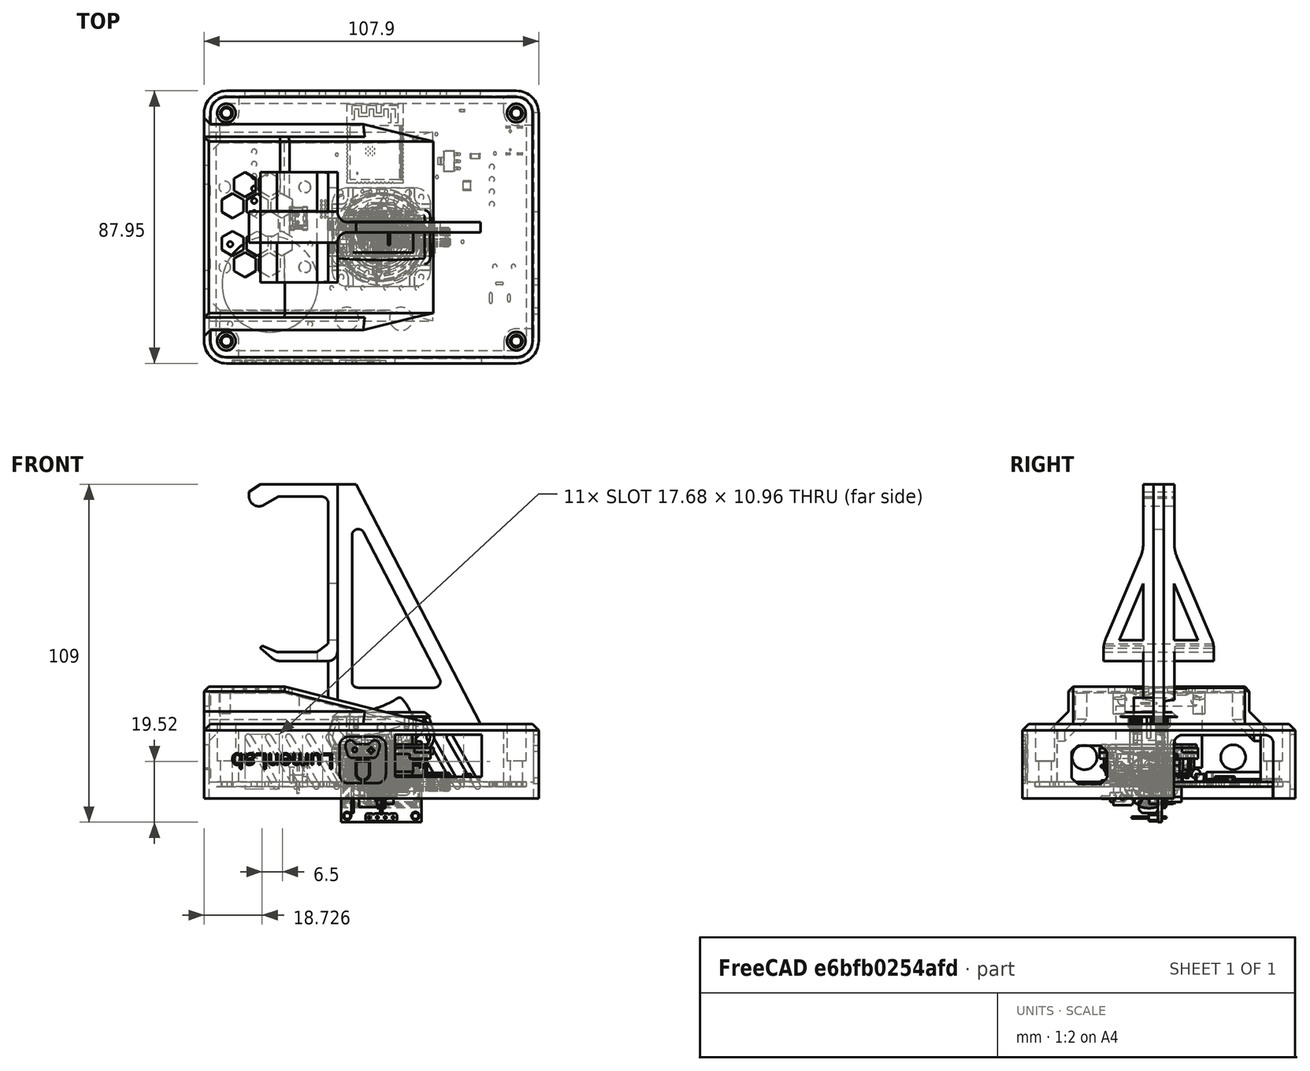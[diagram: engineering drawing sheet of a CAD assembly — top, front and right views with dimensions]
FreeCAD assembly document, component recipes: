
FREECAD ASSEMBLY — COMPONENT RECIPES ("lumenlab-enclosure-redesign")

This assembly document has 9 components, labeled P0..P8 below (a component is one placed body or linked part). 8 of them carry a construction recipe — the FreeCAD feature program that regenerates the part from scratch, quoted from this document or its linked companion documents; the rest are supplied as boundary geometry only. No exploded tour is included for this assembly.
COMPONENT P0 — geometry summary ("lumenlab-pcb001"; no construction recipe available for this part):
  bounding box: 99.9 x 79.9 x 1.6 mm
  tessellated surface: 20,328 triangles
  volume: 11234 mm^3 (88% of its bounding box)
  symmetry: mirror-symmetric across its z mid-plane
COMPONENT P1 — recipe-attached ("lid", modeled in this document).
Construction recipe (the document's own serialized feature program — sketch geometry with constraints, then the solid features built on it; lengths are millimeters unless a unit is written):

FEATURE [PartDesign::SubShapeBinder] Binder
  BindCopyOnChange = 0
  BindMode = 0
  ClaimChildren = false
  Context = -> Body [Binder.]
  Fuse = false
  MakeFace = true
  OffsetFill = false
  OffsetIntersection = false
  OffsetJoinType = 0
  OffsetOpenResult = false
  PartialLoad = false
  Refine = true
  Relative = true
  Support = -> [Board_aaa008]
  _Version = 2
FEATURE [Sketcher::SketchObject] Sketch
  ArcFitTolerance = 1e-06
  AttachmentOffset = pos=(0,0,3.75) rot=(0,0,1;0rad)
  AttachmentSupport = -> [Binder]
  ExternalGeometry = -> [Binder]
  ExternalTypes = [0]
  FullyConstrained = true
  MakeInternals = false
  MapMode = 5
  Placement = pos=(0,0,-5.3502) rot=(1,0,0;3.14159rad)
  _ExternalGeoVersion = 0
  sketch-geometry (10):
    g0: LineSegment StartX=-57.1492 StartY=33.5464 StartZ=0 EndX=-57.1492 EndY=-39.9989 EndZ=0
    g1: LineSegment StartX=-49.9485 StartY=-47.1996 StartZ=0 EndX=43.5501 EndY=-47.1996 EndZ=0
    g2: LineSegment StartX=50.7508 StartY=-39.9989 StartZ=0 EndX=50.7508 EndY=33.5464 EndZ=0
    g3: LineSegment StartX=43.5501 StartY=40.7472 StartZ=0 EndX=-49.9485 EndY=40.7472 EndZ=0
    g4: ArcOfCircle CenterX=-49.9485 CenterY=33.5464 CenterZ=0 NormalX=0 NormalY=0 NormalZ=1 AngleXU=0 Radius=7.20071 StartAngle=1.5708 EndAngle=3.14159
    g5: ArcOfCircle CenterX=-49.9485 CenterY=-39.9989 CenterZ=0 NormalX=0 NormalY=0 NormalZ=1 AngleXU=0 Radius=7.20071 StartAngle=3.14159 EndAngle=4.71239
    g6: ArcOfCircle CenterX=43.5501 CenterY=-39.9989 CenterZ=0 NormalX=0 NormalY=0 NormalZ=1 AngleXU=0 Radius=7.20071 StartAngle=4.71239 EndAngle=6.28319
    g7: ArcOfCircle CenterX=43.5501 CenterY=33.5464 CenterZ=0 NormalX=0 NormalY=0 NormalZ=1 AngleXU=0 Radius=7.20071 StartAngle=1e-16 EndAngle=1.5708
    g8: GeomPoint [constr] X=-57.1492 Y=40.7472 Z=0
    g9: GeomPoint [constr] X=50.7508 Y=-47.1996 Z=0
  constraints (23):
    c: Tangent(g0,g4) = -1.5708
    c: Tangent(g0,g5) = -1.5708
    c: Tangent(g1,g5) = -1.5708
    c: Tangent(g1,g6) = -1.5708
    c: Tangent(g2,g6) = -1.5708
    c: Tangent(g2,g7) = -1.5708
    c: Tangent(g3,g7) = -1.5708
    c: Tangent(g3,g4) = -1.5708
    c: Vertical(g0)
    c: Vertical(g2)
    c: Horizontal(g1)
    c: Horizontal(g3)
    c: Equal(g4,g5)
    c: Equal(g5,g6)
    c: Equal(g6,g7)
    c: PointOnObject(g8,g0)
    c: PointOnObject(g8,g3)
    c: PointOnObject(g9,g1)
    c: PointOnObject(g9,g2)
    c: DistanceX(g0,g-5) = 4  'enclosure-width'
    c: Coincident(g4,g-4)
    c: Distance(g-7,g2) = 4
    c: Distance(g-9,g1) = 4
FEATURE [PartDesign::Pad] Pad
  Direction = (0,0,-1)
  Length = 2
  Length2 = 10
  Profile = -> Sketch
  ReferenceAxis = -> Sketch [N_Axis]
  Refine = true
  SideType = 0
  Suppressed = false
  Type = 0
  Type2 = 0
FEATURE [Sketcher::SketchObject] Sketch001
  ArcFitTolerance = 1e-06
  AttachmentSupport = -> [Pad]
  ExternalGeometry = -> [Binder]
  ExternalTypes = [0]
  FullyConstrained = true
  MakeInternals = false
  MapMode = 5
  Placement = pos=(0,0,-5.3502) rot=(0,0,1;0rad)
  _ExternalGeoVersion = 0
  sketch-geometry (20):
    g0: LineSegment StartX=-55.15 StartY=39.9996 StartZ=0 EndX=-55.15 EndY=-33.5498 EndZ=0
    g1: LineSegment StartX=-49.95 StartY=-38.7498 StartZ=0 EndX=43.551 EndY=-38.7498 EndZ=0
    g2: LineSegment StartX=48.751 StartY=-33.5498 StartZ=0 EndX=48.751 EndY=39.9996 EndZ=0
    g3: LineSegment StartX=43.551 StartY=45.1996 StartZ=0 EndX=-49.95 EndY=45.1996 EndZ=0
    g4: ArcOfCircle CenterX=-49.95 CenterY=39.9996 CenterZ=0 NormalX=0 NormalY=0 NormalZ=1 AngleXU=0 Radius=5.19999 StartAngle=1.5708 EndAngle=3.14159
    g5: ArcOfCircle CenterX=-49.95 CenterY=-33.5498 CenterZ=0 NormalX=0 NormalY=0 NormalZ=1 AngleXU=0 Radius=5.19999 StartAngle=3.14159 EndAngle=4.71239
    g6: ArcOfCircle CenterX=43.551 CenterY=-33.5498 CenterZ=0 NormalX=0 NormalY=0 NormalZ=1 AngleXU=0 Radius=5.19999 StartAngle=4.71239 EndAngle=6.28319
    g7: ArcOfCircle CenterX=43.551 CenterY=39.9996 CenterZ=0 NormalX=0 NormalY=0 NormalZ=1 AngleXU=0 Radius=5.19999 StartAngle=5e-16 EndAngle=1.5708
    g8: GeomPoint [constr] X=-55.15 Y=45.1996 Z=0
    g9: GeomPoint [constr] X=48.751 Y=-38.7498 Z=0
    g10: LineSegment StartX=-53.35 StartY=39.9996 StartZ=0 EndX=-53.35 EndY=-33.5498 EndZ=0
    g11: LineSegment StartX=-49.95 StartY=-36.9498 StartZ=0 EndX=43.551 EndY=-36.9498 EndZ=0
    g12: LineSegment StartX=46.951 StartY=-33.5498 StartZ=0 EndX=46.951 EndY=39.9996 EndZ=0
    g13: LineSegment StartX=43.551 StartY=43.3996 StartZ=0 EndX=-49.95 EndY=43.3996 EndZ=0
    g14: ArcOfCircle CenterX=-49.95 CenterY=39.9996 CenterZ=0 NormalX=0 NormalY=0 NormalZ=1 AngleXU=0 Radius=3.39999 StartAngle=1.5708 EndAngle=3.14159
    g15: ArcOfCircle CenterX=-49.95 CenterY=-33.5498 CenterZ=0 NormalX=0 NormalY=0 NormalZ=1 AngleXU=0 Radius=3.39999 StartAngle=3.14159 EndAngle=4.71239
    g16: ArcOfCircle CenterX=43.551 CenterY=-33.5498 CenterZ=0 NormalX=0 NormalY=0 NormalZ=1 AngleXU=0 Radius=3.39999 StartAngle=4.71239 EndAngle=6.28319
    g17: ArcOfCircle CenterX=43.551 CenterY=39.9996 CenterZ=0 NormalX=0 NormalY=0 NormalZ=1 AngleXU=0 Radius=3.39999 StartAngle=0 EndAngle=1.5708
    g18: GeomPoint [constr] X=-53.35 Y=43.3996 Z=0
    g19: GeomPoint [constr] X=46.951 Y=-36.9498 Z=0
  constraints (46):
    c: Tangent(g0,g4) = -1.5708
    c: Tangent(g0,g5) = -1.5708
    c: Tangent(g1,g5) = -1.5708
    c: Tangent(g1,g6) = -1.5708
    c: Tangent(g2,g6) = -1.5708
    c: Tangent(g2,g7) = -1.5708
    c: Tangent(g3,g7) = -1.5708
    c: Tangent(g3,g4) = -1.5708
    c: Vertical(g0)
    c: Vertical(g2)
    c: Horizontal(g1)
    c: Horizontal(g3)
    c: Equal(g4,g5)
    c: Equal(g5,g6)
    c: Equal(g6,g7)
    c: PointOnObject(g8,g0)
    c: PointOnObject(g8,g3)
    c: PointOnObject(g9,g1)
    c: PointOnObject(g9,g2)
    c: DistanceX(g0,g-5) = 2
    c: Coincident(g4,g-4)
    c: DistanceX(g-7,g2) = 2
    c: DistanceY(g1,g-9) = 2
    c: Tangent(g10,g14) = -1.5708
    c: Tangent(g10,g15) = -1.5708
    c: Tangent(g11,g15) = -1.5708
    c: Tangent(g11,g16) = -1.5708
    c: Tangent(g12,g16) = -1.5708
    c: Tangent(g12,g17) = -1.5708
    c: Tangent(g13,g17) = -1.5708
    c: Tangent(g13,g14) = -1.5708
    c: Vertical(g10)
    c: Vertical(g12)
    c: Horizontal(g11)
    c: Horizontal(g13)
    c: Equal(g14,g15)
    c: Equal(g15,g16)
    c: Equal(g16,g17)
    c: PointOnObject(g18,g10)
    c: PointOnObject(g18,g13)
    c: PointOnObject(g19,g11)
    c: PointOnObject(g19,g12)
    c: DistanceX(g10,g-5) = 0.2
    c: DistanceX(g-7,g12) = 0.2
    c: DistanceY(g11,g-9) = 0.2
    c: Coincident(g14,g4)
FEATURE [PartDesign::Pad] Pad001
  BaseFeature = -> Pad
  Direction = (0,0,1)
  Length = 5
  Length2 = 10
  Profile = -> Sketch001
  ReferenceAxis = -> Sketch001 [N_Axis]
  Refine = true
  SideType = 0
  Suppressed = false
  Type = 0
  Type2 = 0
FEATURE [Sketcher::SketchObject] Sketch002
  ArcFitTolerance = 1e-06
  ExternalGeometry = -> [Binder,Pad001]
  ExternalTypes = [0]
  FullyConstrained = true
  MakeInternals = false
  MapMode = 5
  Placement = pos=(0,0,-2) rot=(1,0,0;3.14159rad)
  _ExternalGeoVersion = 0
  sketch-geometry (10):
    g0: LineSegment StartX=-53.1492 StartY=29.5498 StartZ=0 EndX=-53.35 EndY=29.5498 EndZ=0
    g1: LineSegment StartX=-45.95 StartY=36.7473 StartZ=0 EndX=-45.95 EndY=36.9498 EndZ=0
    g2: LineSegment StartX=-45.95 StartY=36.9498 StartZ=0 EndX=-49.95 EndY=36.9498 EndZ=0
    g3: LineSegment StartX=-53.35 StartY=29.5498 StartZ=0 EndX=-53.35 EndY=33.5498 EndZ=0
    g4: ArcOfCircle CenterX=-49.95 CenterY=33.5498 CenterZ=0 NormalX=0 NormalY=0 NormalZ=1 AngleXU=0 Radius=3.39999 StartAngle=1.5708 EndAngle=3.14159
    g5: LineSegment StartX=-53.1492 StartY=29.5498 StartZ=0 EndX=-48.6466 EndY=29.5498 EndZ=0
    g6: ArcOfCircle CenterX=-48.6466 CenterY=30.4451 CenterZ=0 NormalX=0 NormalY=0 NormalZ=1 AngleXU=0 Radius=0.895293 StartAngle=4.71239 EndAngle=5.38086
    g7: LineSegment StartX=-48.0918 StartY=29.7425 StartZ=0 EndX=-46.138 EndY=31.2855 EndZ=0
    g8: ArcOfCircle CenterX=-46.4444 CenterY=31.6735 CenterZ=0 NormalX=0 NormalY=0 NormalZ=1 AngleXU=0 Radius=0.494368 StartAngle=5.38086 EndAngle=6.28319
    g9: LineSegment StartX=-45.95 StartY=31.6735 StartZ=0 EndX=-45.95 EndY=36.7473 EndZ=0
  constraints (24):
    c: PointOnObject(g0,g-8)
    c: Horizontal(g0)
    c: PointOnObject(g1,g-7)
    c: Vertical(g1)
    c: Coincident(g2,g1)
    c: Coincident(g2,g-9)
    c: Coincident(g3,g0)
    c: Coincident(g3,g-9)
    c: Coincident(g4,g2)
    c: Coincident(g4,g3)
    c: PointOnObject(g0,g-10)
    c: PointOnObject(g1,g-11)
    c: DistanceY(g3,g3) = 4
    c: DistanceX(g2,g2) = 4
    c: Equal(g4,g-9)
    c: Coincident(g0,g5)
    c: Tangent(g5,g6) = -1.5708
    c: Tangent(g6,g7) = -1.5708
    c: Tangent(g7,g8) = -1.5708
    c: Tangent(g8,g9) = -1.5708
    c: Vertical(g9)
    c: Coincident(g9,g1)
    c: Horizontal(g5)
    c: Block(g7)
FEATURE [PartDesign::Pad] Pad002
  BaseFeature = -> Pad001
  Direction = (0,-1e-16,-1)
  Length = 10
  Length2 = 10
  Profile = -> Sketch002
  ReferenceAxis = -> Sketch002 [N_Axis]
  Refine = true
  SideType = 0
  Suppressed = false
  Type = 2
  Type2 = 0
FEATURE [PartDesign::Plane] DatumPlane
  AttachmentOffset = pos=(0,0,0) rot=(1,0,0;1.5708rad)
  AttachmentSupport = -> [Pad002]
  Length = 122.59
  MapMode = 45
  Placement = pos=(-3.1995,3.22491,-2.8502) rot=(1,0,0;1.5708rad)
  ResizeMode = 0
  Width = 64.6901
  expr: .AttachmentOffset.Rotation.Pitch = 0
FEATURE [PartDesign::Plane] DatumPlane001
  AttachmentOffset = pos=(0,0,0) rot=(1,0,0;1.5708rad)
  AttachmentSupport = -> [Pad002]
  Length = 101.209
  MapMode = 45
  Placement = pos=(-3.1995,3.22491,-2.8502) rot=(0.57735,0.57735,0.57735;2.0944rad)
  ResizeMode = 0
  Width = 63.2625
FEATURE [PartDesign::Line] DatumLine
  AttacherType = Attacher::AttachEngineLine
  AttachmentSupport = -> [DatumPlane001,DatumPlane]
  Length = 20
  MapMode = 30
  Placement = pos=(-3.1995,3.22491,-2.8502) rot=(0,1,0;3.14159rad)
  ResizeMode = 0
FEATURE [PartDesign::Mirrored] Mirrored
  BaseFeature = -> Pad002
  MirrorPlane = -> DatumPlane
  Originals = -> [Pad002]
  Refine = true
  Suppressed = false
  TransformMode = 0
FEATURE [PartDesign::Mirrored] Mirrored001
  BaseFeature = -> Mirrored
  MirrorPlane = -> DatumPlane001
  Originals = -> [Pad002]
  Refine = true
  Suppressed = false
  TransformMode = 0
FEATURE [PartDesign::PolarPattern] PolarPattern
  Angle = 360
  Axis = -> DatumLine
  BaseFeature = -> Mirrored001
  Mode = 0
  Occurrences = 2
  Offset = 120
  Originals = -> [Pad002]
  Refine = true
  Reversed = true
  SpacingPattern = [0]
  Spacings = [-1]
  Suppressed = false
  TransformMode = 0
FEATURE [Sketcher::SketchObject] Sketch003
  ArcFitTolerance = 1e-06
  AttachmentSupport = -> [PolarPattern]
  ExternalTypes = [0]
  FullyConstrained = true
  MakeInternals = false
  MapMode = 5
  Placement = pos=(0,0,-2) rot=(0,0,1;0rad)
  _ExternalGeoVersion = 0
  sketch-geometry (1):
    g0: Circle CenterX=-49.95 CenterY=-33.5498 CenterZ=0 NormalX=0 NormalY=0 NormalZ=1 AngleXU=0 Radius=2.425
  constraints (2):
    c: Coincident(g0,g-3)
    c: Diameter(g0) = 4.85
FEATURE [PartDesign::Pocket] Pocket
  BaseFeature = -> PolarPattern
  Direction = (0,0,-1)
  Length = 4.35
  Length2 = 5
  Profile = -> Sketch003
  ReferenceAxis = -> Sketch003 [N_Axis]
  Refine = true
  SideType = 0
  Suppressed = false
  Type = 0
  Type2 = 0
FEATURE [PartDesign::Mirrored] Mirrored002
  BaseFeature = -> Pocket
  MirrorPlane = -> DatumPlane
  Originals = -> [Pocket]
  Refine = true
  Suppressed = false
  TransformMode = 0
FEATURE [PartDesign::Mirrored] Mirrored003
  BaseFeature = -> Mirrored002
  MirrorPlane = -> DatumPlane001
  Originals = -> [Pocket]
  Refine = true
  Suppressed = false
  TransformMode = 0
FEATURE [PartDesign::PolarPattern] PolarPattern001
  Angle = 360
  Axis = -> DatumLine
  BaseFeature = -> Mirrored003
  Mode = 0
  Occurrences = 2
  Offset = 120
  Originals = -> [Pocket]
  Refine = true
  SpacingPattern = [0]
  Spacings = [-1]
  Suppressed = false
  TransformMode = 0
FEATURE [Sketcher::SketchObject] Sketch018
  ArcFitTolerance = 1e-06
  ExternalTypes = [0]
  FullyConstrained = true
  MakeInternals = false
  MapMode = 5
  Placement = pos=(48.751,0,0) rot=(0.57735,0.57735,0.57735;2.0944rad)
  _ExternalGeoVersion = 0
  sketch-geometry (4):
    g0: LineSegment StartX=8.59847 StartY=-0.350198 StartZ=0 EndX=8.59847 EndY=-5.3502 EndZ=0
    g1: LineSegment StartX=8.59847 StartY=-5.3502 StartZ=0 EndX=39.3209 EndY=-5.3502 EndZ=0
    g2: LineSegment StartX=39.3209 StartY=-0.350198 StartZ=0 EndX=8.59847 EndY=-0.350198 EndZ=0
    g3: LineSegment StartX=39.3209 StartY=-5.3502 StartZ=0 EndX=39.3209 EndY=-0.350198 EndZ=0
  constraints (12):
    c: Coincident(g0,g1)
    c: Coincident(g2,g0)
    c: Vertical(g0)
    c: Horizontal(g1)
    c: Horizontal(g2)
    c: PointOnObject(g0,g-5)
    c: Distance(g0,g-3) = 0.1
    c: DistanceY(g0,g0) = 5
    c: Vertical(g3)
    c: Distance(g3,g-7) = 3.65
    c: Coincident(g1,g3)
    c: Coincident(g3,g2)
FEATURE [PartDesign::Pad] Pad007
  BaseFeature = -> PolarPattern001
  Direction = (1,1e-16,-1e-16)
  Length = 2
  Length2 = 10
  Profile = -> Sketch018
  ReferenceAxis = -> Sketch018 [N_Axis]
  Refine = true
  SideType = 0
  Suppressed = false
  Type = 0
  Type2 = 0
FEATURE [Sketcher::SketchObject] Sketch019
  ArcFitTolerance = 1e-06
  AttachmentSupport = -> [Pad007]
  ExternalTypes = [0]
  FullyConstrained = true
  MakeInternals = false
  MapMode = 5
  Placement = pos=(48.751,0,0) rot=(0.57735,0.57735,0.57735;2.0944rad)
  _ExternalGeoVersion = 0
  sketch-geometry (10):
    g0: LineSegment StartX=22.9809 StartY=2.01 StartZ=0 EndX=22.9809 EndY=1.3 EndZ=0
    g1: LineSegment StartX=28.0309 StartY=-3.75 StartZ=0 EndX=34.3709 EndY=-3.75 EndZ=0
    g2: LineSegment StartX=39.4209 StartY=1.3 StartZ=0 EndX=39.4209 EndY=2.01 EndZ=0
    g3: LineSegment StartX=34.3709 StartY=7.06 StartZ=0 EndX=28.0309 EndY=7.06 EndZ=0
    g4: ArcOfCircle CenterX=28.0309 CenterY=2.01 CenterZ=0 NormalX=0 NormalY=0 NormalZ=1 AngleXU=0 Radius=5.05 StartAngle=1.5708 EndAngle=3.14159
    g5: ArcOfCircle CenterX=28.0309 CenterY=1.3 CenterZ=0 NormalX=0 NormalY=0 NormalZ=1 AngleXU=0 Radius=5.05 StartAngle=3.14159 EndAngle=4.71239
    g6: ArcOfCircle CenterX=34.3709 CenterY=1.3 CenterZ=0 NormalX=0 NormalY=0 NormalZ=1 AngleXU=0 Radius=5.05 StartAngle=4.71239 EndAngle=6.28319
    g7: ArcOfCircle CenterX=34.3709 CenterY=2.01 CenterZ=0 NormalX=0 NormalY=0 NormalZ=1 AngleXU=0 Radius=5.05 StartAngle=0 EndAngle=1.5708
    g8: GeomPoint [constr] X=22.9809 Y=7.06 Z=0
    g9: GeomPoint [constr] X=39.4209 Y=-3.75 Z=0
  constraints (21):
    c: Tangent(g0,g4) = -1.5708
    c: Tangent(g0,g5) = -1.5708
    c: Tangent(g1,g5) = -1.5708
    c: Tangent(g1,g6) = -1.5708
    c: Tangent(g2,g6) = -1.5708
    c: Tangent(g2,g7) = -1.5708
    c: Tangent(g3,g7) = -1.5708
    c: Tangent(g3,g4) = -1.5708
    c: Vertical(g0)
    c: Vertical(g2)
    c: Horizontal(g1)
    c: Horizontal(g3)
    c: Equal(g5,g6)
    c: PointOnObject(g8,g0)
    c: PointOnObject(g8,g3)
    c: PointOnObject(g9,g1)
    c: PointOnObject(g9,g2)
    c: Coincident(g4,g-4)
    c: Coincident(g5,g-10)
    c: Coincident(g7,g-6)
    c: DistanceX(g0,g-4) = 3.75
FEATURE [PartDesign::Pocket] Pocket011
  BaseFeature = -> Pad007
  Direction = (-1,0,0)
  Length = 4
  Length2 = 5
  Profile = -> Sketch019
  ReferenceAxis = -> Sketch019 [N_Axis]
  Refine = true
  SideType = 2
  Suppressed = false
  Type = 0
  Type2 = 0
FEATURE [PartDesign::Chamfer] Chamfer006
  Angle = 45
  Base = -> Pocket011 [Edge30,Edge29,Edge28,Edge31,Edge32,Edge10,Edge4,Edge7]
  BaseFeature = -> Pocket011
  ChamferType = 0
  FlipDirection = false
  Refine = true
  Size = 1
  Size2 = 1
  SupportTransform = false
  Suppressed = false
  UseAllEdges = false
FEATURE [PartDesign::Body] Body  label="lid"
  AllowCompound = false
  Group = -> [Binder,Sketch,Pad,Sketch001,Pad001,Sketch002,Pad002,DatumPlane,Mirrored,DatumPlane001,Mirrored001,DatumLine,PolarPattern,Sketch003,Pocket,Mirrored002,Mirrored003,PolarPattern001,Sketch018,Pad007,Sketch019,Pocket011,Chamfer006]
  Origin = -> Origin032
  Tip = -> Chamfer006
COMPONENT P2 — recipe-attached ("Body", modeled in this document).
Construction recipe (the document's own serialized feature program — sketch geometry with constraints, then the solid features built on it; lengths are millimeters unless a unit is written):

FEATURE [PartDesign::SubShapeBinder] Binder001
  BindCopyOnChange = 0
  BindMode = 0
  ClaimChildren = false
  Context = -> Body001 [Binder001.]
  Fuse = false
  MakeFace = true
  OffsetFill = false
  OffsetIntersection = false
  OffsetJoinType = 0
  OffsetOpenResult = false
  PartialLoad = false
  Refine = true
  Relative = true
  Support = -> [Board_aaa008]
  _Version = 2
FEATURE [Sketcher::SketchObject] Sketch010
  ArcFitTolerance = 1e-06
  AttachmentOffset = pos=(0,0,3.75) rot=(0,0,1;0rad)
  AttachmentSupport = -> [Binder001]
  ExternalGeometry = -> [Binder001]
  ExternalTypes = [0]
  FullyConstrained = true
  MakeInternals = false
  MapMode = 5
  Placement = pos=(0,0,-5.3502) rot=(1,0,0;3.14159rad)
  _ExternalGeoVersion = 0
  sketch-geometry (19):
    g0: LineSegment StartX=-57.1492 StartY=33.5464 StartZ=0 EndX=-57.1492 EndY=-39.9996 EndZ=0
    g1: LineSegment StartX=-49.9492 StartY=-47.1996 StartZ=0 EndX=43.5508 EndY=-47.1996 EndZ=0
    g2: LineSegment StartX=50.7508 StartY=-39.9996 StartZ=0 EndX=50.7508 EndY=33.5464 EndZ=0
    g3: LineSegment StartX=43.5508 StartY=40.7464 StartZ=0 EndX=-49.9492 EndY=40.7464 EndZ=0
    g4: ArcOfCircle CenterX=-49.9492 CenterY=33.5464 CenterZ=0 NormalX=0 NormalY=0 NormalZ=1 AngleXU=0 Radius=7.19996 StartAngle=1.5708 EndAngle=3.14159
    g5: ArcOfCircle CenterX=-49.9492 CenterY=-39.9996 CenterZ=0 NormalX=0 NormalY=0 NormalZ=1 AngleXU=0 Radius=7.19996 StartAngle=3.14159 EndAngle=4.71239
    g6: ArcOfCircle CenterX=43.5508 CenterY=-39.9996 CenterZ=0 NormalX=0 NormalY=0 NormalZ=1 AngleXU=0 Radius=7.19996 StartAngle=4.71239 EndAngle=6.28319
    g7: ArcOfCircle CenterX=43.5508 CenterY=33.5464 CenterZ=0 NormalX=0 NormalY=0 NormalZ=1 AngleXU=0 Radius=7.19996 StartAngle=0 EndAngle=1.5708
    g8: GeomPoint [constr] X=-57.1492 Y=40.7464 Z=0
    g9: GeomPoint [constr] X=50.7508 Y=-47.1996 Z=0
    g10: LineSegment StartX=-49.9492 StartY=-45.5996 StartZ=0 EndX=43.5508 EndY=-45.5996 EndZ=0
    g11: LineSegment StartX=49.1508 StartY=-39.9996 StartZ=0 EndX=49.1508 EndY=33.5464 EndZ=0
    g12: LineSegment StartX=43.5508 StartY=39.1464 StartZ=0 EndX=-49.9492 EndY=39.1464 EndZ=0
    g13: LineSegment StartX=-55.5492 StartY=33.5464 StartZ=0 EndX=-55.5492 EndY=-39.9996 EndZ=0
    g14: ArcOfCircle CenterX=-49.9492 CenterY=-39.9996 CenterZ=0 NormalX=0 NormalY=0 NormalZ=1 AngleXU=0 Radius=5.59996 StartAngle=3.14159 EndAngle=4.71239
    g15: ArcOfCircle CenterX=43.5508 CenterY=-39.9996 CenterZ=0 NormalX=0 NormalY=0 NormalZ=1 AngleXU=0 Radius=5.59996 StartAngle=4.71239 EndAngle=6.28319
    g16: ArcOfCircle CenterX=43.5508 CenterY=33.5464 CenterZ=0 NormalX=0 NormalY=0 NormalZ=1 AngleXU=0 Radius=5.59996 StartAngle=4e-16 EndAngle=1.5708
    g17: ArcOfCircle CenterX=-49.9492 CenterY=33.5464 CenterZ=0 NormalX=0 NormalY=0 NormalZ=1 AngleXU=0 Radius=5.59996 StartAngle=1.5708 EndAngle=3.14159
    g18: GeomPoint [constr] X=-55.5492 Y=-45.5996 Z=0
  constraints (43):
    c: Tangent(g0,g4) = -1.5708
    c: Tangent(g0,g5) = -1.5708
    c: Tangent(g1,g5) = -1.5708
    c: Tangent(g1,g6) = -1.5708
    c: Tangent(g2,g6) = -1.5708
    c: Tangent(g2,g7) = -1.5708
    c: Tangent(g3,g7) = -1.5708
    c: Tangent(g3,g4) = -1.5708
    c: Vertical(g0)
    c: Vertical(g2)
    c: Horizontal(g1)
    c: Horizontal(g3)
    c: Equal(g4,g5)
    c: Equal(g5,g6)
    c: Equal(g6,g7)
    c: PointOnObject(g8,g0)
    c: PointOnObject(g8,g3)
    c: PointOnObject(g9,g1)
    c: PointOnObject(g9,g2)
    c: Distance(g0,g-3) = 4
    c: Coincident(g-10,g4)
    c: Distance(g2,g-7) = 4
    c: Distance(g1,g-4) = 4
    c: Tangent(g10,g14) = -1.5708
    c: Tangent(g10,g15) = -1.5708
    c: Tangent(g11,g15) = -1.5708
    c: Tangent(g11,g16) = -1.5708
    c: Tangent(g12,g16) = -1.5708
    c: Tangent(g12,g17) = -1.5708
    c: Tangent(g13,g17) = -1.5708
    c: Tangent(g13,g14) = -1.5708
    c: Horizontal(g10)
    c: Horizontal(g12)
    c: Vertical(g11)
    c: Vertical(g13)
    c: Equal(g14,g15)
    c: Equal(g15,g16)
    c: Equal(g16,g17)
    c: PointOnObject(g18,g10)
    c: PointOnObject(g18,g13)
    c: Distance(g0,g13) = 1.6
    c: Coincident(g14,g5)
    c: Coincident(g16,g7)
FEATURE [PartDesign::Pad] Pad003
  Direction = (0,0,-1)
  Length = 22
  Length2 = 10
  Profile = -> Sketch010
  ReferenceAxis = -> Sketch010 [N_Axis]
  Refine = true
  Reversed = true
  SideType = 0
  Suppressed = false
  Type = 0
  Type2 = 0
FEATURE [Sketcher::SketchObject] Sketch011
  ArcFitTolerance = 1e-06
  AttachmentSupport = -> [Pad003]
  ExternalGeometry = -> [Pad003]
  ExternalTypes = [0]
  FullyConstrained = true
  MakeInternals = false
  MapMode = 5
  Placement = pos=(0,0,16.6498) rot=(0,0,1;0rad)
  _ExternalGeoVersion = 0
  sketch-geometry (10):
    g0: LineSegment StartX=-57.1492 StartY=39.9996 StartZ=0 EndX=-57.1492 EndY=-33.5464 EndZ=0
    g1: LineSegment StartX=-49.9492 StartY=-40.7464 StartZ=0 EndX=43.5508 EndY=-40.7464 EndZ=0
    g2: LineSegment StartX=50.7508 StartY=-33.5464 StartZ=0 EndX=50.7508 EndY=39.9996 EndZ=0
    g3: LineSegment StartX=43.5508 StartY=47.1996 StartZ=0 EndX=-49.9492 EndY=47.1996 EndZ=0
    g4: ArcOfCircle CenterX=-49.9492 CenterY=39.9996 CenterZ=0 NormalX=0 NormalY=0 NormalZ=1 AngleXU=0 Radius=7.19996 StartAngle=1.5708 EndAngle=3.14159
    g5: ArcOfCircle CenterX=-49.9492 CenterY=-33.5464 CenterZ=0 NormalX=0 NormalY=0 NormalZ=1 AngleXU=0 Radius=7.19996 StartAngle=3.14159 EndAngle=4.71239
    g6: ArcOfCircle CenterX=43.5508 CenterY=-33.5464 CenterZ=0 NormalX=0 NormalY=0 NormalZ=1 AngleXU=0 Radius=7.19996 StartAngle=4.71239 EndAngle=6.28319
    g7: ArcOfCircle CenterX=43.5508 CenterY=39.9996 CenterZ=0 NormalX=0 NormalY=0 NormalZ=1 AngleXU=0 Radius=7.19996 StartAngle=0 EndAngle=1.5708
    g8: GeomPoint [constr] X=-57.1492 Y=47.1996 Z=0
    g9: GeomPoint [constr] X=50.7508 Y=-40.7464 Z=0
  constraints (20):
    c: Tangent(g0,g4) = -1.5708
    c: Tangent(g0,g5) = -1.5708
    c: Tangent(g1,g5) = -1.5708
    c: Tangent(g1,g6) = -1.5708
    c: Tangent(g2,g6) = -1.5708
    c: Tangent(g2,g7) = -1.5708
    c: Tangent(g3,g7) = -1.5708
    c: Tangent(g3,g4) = -1.5708
    c: Vertical(g2)
    c: Horizontal(g1)
    c: Equal(g4,g5)
    c: Equal(g5,g6)
    c: PointOnObject(g8,g0)
    c: PointOnObject(g8,g3)
    c: PointOnObject(g9,g1)
    c: PointOnObject(g9,g2)
    c: Coincident(g-5,g0)
    c: Coincident(g3,g-4)
    c: Coincident(g3,g-6)
    c: Coincident(g1,g-9)
FEATURE [PartDesign::Pad] Pad004
  BaseFeature = -> Pad003
  Direction = (0,0,1)
  Length = 2
  Length2 = 10
  Profile = -> Sketch011
  ReferenceAxis = -> Sketch011 [N_Axis]
  Refine = true
  SideType = 0
  Suppressed = false
  Type = 0
  Type2 = 0
FEATURE [Sketcher::SketchObject] Sketch013
  ArcFitTolerance = 1e-06
  ExternalTypes = [0]
  FullyConstrained = false
  MakeInternals = false
  MapMode = 5
  Placement = pos=(50.7508,0,3.061e-13) rot=(0.57735,0.57735,0.57735;2.0944rad)
  _ExternalGeoVersion = 0
  sketch-geometry (6):
    g0: LineSegment StartX=8.16428 StartY=12.4216 StartZ=0 EndX=8.16428 EndY=-5.3502 EndZ=0
    g1: LineSegment StartX=40.1456 StartY=12.4216 StartZ=0 EndX=40.1456 EndY=-5.3502 EndZ=0
    g2: LineSegment StartX=40.1456 StartY=-5.3502 StartZ=0 EndX=8.16428 EndY=-5.3502 EndZ=0
    g3: LineSegment StartX=10.823 StartY=15.0803 StartZ=0 EndX=37.4869 EndY=15.0803 EndZ=0
    g4: ArcOfCircle CenterX=10.823 CenterY=12.4216 CenterZ=0 NormalX=0 NormalY=0 NormalZ=1 AngleXU=0 Radius=2.6587 StartAngle=1.5708 EndAngle=3.14159
    g5: ArcOfCircle CenterX=37.4869 CenterY=12.4216 CenterZ=0 NormalX=0 NormalY=0 NormalZ=1 AngleXU=0 Radius=2.6587 StartAngle=1e-16 EndAngle=1.5708
  constraints (16):
    c: Vertical(g1)
    c: Coincident(g1,g2)
    c: PointOnObject(g0,g-10)
    c: Horizontal(g2)
    c: Coincident(g2,g0)
    c: Horizontal(g3)
    c: Vertical(g0)
    c: Coincident(g4,g0)
    c: Coincident(g3,g4)
    c: Coincident(g5,g3)
    c: Vertical(g3,g4)
    c: Horizontal(g0,g4)
    c: Coincident(g1,g5)
    c: Equal(g4,g5)
    c: Vertical(g3,g5)
    c: Horizontal(g5,g1)
FEATURE [PartDesign::Pocket] Pocket008
  BaseFeature = -> Pad004
  Direction = (-1,-1e-16,-5.9e-15)
  Length = 5
  Length2 = 5
  Profile = -> Sketch013
  ReferenceAxis = -> Sketch013 [N_Axis]
  Refine = true
  SideType = 0
  Suppressed = false
  Type = 2
  Type2 = 0
FEATURE [Sketcher::SketchObject] Sketch014
  ArcFitTolerance = 1e-06
  ExternalTypes = [0]
  FullyConstrained = true
  MakeInternals = false
  MapMode = 5
  Placement = pos=(50.7508,0,2.944e-13) rot=(0.57735,0.57735,0.57735;2.0944rad)
  _ExternalGeoVersion = 0
  sketch-geometry (4):
    g0: LineSegment StartX=-24.8504 StartY=11.7 StartZ=0 EndX=-24.8504 EndY=-0.7 EndZ=0
    g1: LineSegment StartX=-24.8504 StartY=-0.7 StartZ=0 EndX=-13.4504 EndY=-0.7 EndZ=0
    g2: LineSegment StartX=-13.4504 StartY=-0.7 StartZ=0 EndX=-13.4504 EndY=11.7 EndZ=0
    g3: LineSegment StartX=-13.4504 StartY=11.7 StartZ=0 EndX=-24.8504 EndY=11.7 EndZ=0
  constraints (12):
    c: Coincident(g0,g1)
    c: Coincident(g1,g2)
    c: Coincident(g2,g3)
    c: Coincident(g3,g0)
    c: Vertical(g0)
    c: Vertical(g2)
    c: Horizontal(g1)
    c: Horizontal(g3)
    c: Distance(g-5,g0) = 1
    c: Distance(g-6,g2) = 2
    c: Distance(g3,g-5) = 1
    c: Distance(g-4,g1) = 1
FEATURE [PartDesign::Pocket] Pocket009
  BaseFeature = -> Pocket008
  Direction = (-1,0,-5.8e-15)
  Length = 5
  Length2 = 5
  Profile = -> Sketch014
  ReferenceAxis = -> Sketch014 [N_Axis]
  Refine = true
  SideType = 0
  Suppressed = false
  Type = 2
  Type2 = 0
FEATURE [PartDesign::Chamfer] Chamfer004
  Angle = 45
  Base = -> Pocket009 [Edge57,Edge60,Edge55,Edge58]
  BaseFeature = -> Pocket009
  ChamferType = 0
  FlipDirection = false
  Refine = true
  Size = 2
  Size2 = 1
  SupportTransform = false
  Suppressed = false
  UseAllEdges = false
FEATURE [Sketcher::SketchObject] Sketch015
  ArcFitTolerance = 1e-06
  ExternalGeometry = -> [Binder001,Chamfer004]
  ExternalTypes = [0]
  FullyConstrained = true
  MakeInternals = false
  MapMode = 5
  Placement = pos=(0,0,0) rot=(1,0,0;3.14159rad)
  _ExternalGeoVersion = 0
  sketch-geometry (30):
    g0: LineSegment StartX=-55.5492 StartY=29.5464 StartZ=0 EndX=-49.9492 EndY=29.5464 EndZ=0
    g1: ArcOfCircle CenterX=-49.9492 CenterY=33.5464 CenterZ=0 NormalX=0 NormalY=0 NormalZ=1 AngleXU=0 Radius=4 StartAngle=4.71239 EndAngle=6.28319
    g2: LineSegment StartX=-45.9492 StartY=33.5464 StartZ=0 EndX=-45.9492 EndY=39.1464 EndZ=0
    g3: LineSegment StartX=-45.9492 StartY=39.1464 StartZ=0 EndX=-49.9492 EndY=39.1464 EndZ=0
    g4: ArcOfCircle CenterX=-49.9492 CenterY=33.5464 CenterZ=0 NormalX=0 NormalY=0 NormalZ=1 AngleXU=0 Radius=5.59996 StartAngle=1.5708 EndAngle=3.14159
    g5: LineSegment StartX=-55.5492 StartY=33.5464 StartZ=0 EndX=-55.5492 EndY=29.5464 EndZ=0
    g6: Circle CenterX=-49.9492 CenterY=33.5464 CenterZ=0 NormalX=0 NormalY=0 NormalZ=1 AngleXU=0 Radius=2
    g7: Circle CenterX=-49.9492 CenterY=-39.9996 CenterZ=0 NormalX=0 NormalY=0 NormalZ=1 AngleXU=0 Radius=2
    g8: LineSegment StartX=-49.9492 StartY=-35.9996 StartZ=0 EndX=-55.5492 EndY=-35.9996 EndZ=0
    g9: LineSegment [constr] StartX=-55.5492 StartY=-39.9996 StartZ=0 EndX=-55.5492 EndY=-4.52586 EndZ=0
    g10: LineSegment StartX=-55.5492 StartY=-35.9996 StartZ=0 EndX=-55.5492 EndY=-39.9996 EndZ=0
    g11: ArcOfCircle CenterX=-49.9492 CenterY=-39.9996 CenterZ=0 NormalX=0 NormalY=0 NormalZ=1 AngleXU=0 Radius=5.59996 StartAngle=3.14159 EndAngle=4.71239
    g12: LineSegment StartX=-49.9492 StartY=-45.5996 StartZ=0 EndX=-45.9492 EndY=-45.5996 EndZ=0
    g13: LineSegment [constr] StartX=49.1508 StartY=-39.9996 StartZ=0 EndX=49.1508 EndY=-8.19439 EndZ=0
    g14: LineSegment StartX=43.5508 StartY=-45.5996 StartZ=0 EndX=39.5508 EndY=-45.5996 EndZ=0
    g15: LineSegment StartX=43.5508 StartY=-35.9996 StartZ=0 EndX=49.1508 EndY=-35.9996 EndZ=0
    g16: LineSegment StartX=49.1508 StartY=-35.9996 StartZ=0 EndX=49.1508 EndY=-39.9996 EndZ=0
    g17: ArcOfCircle CenterX=43.5508 CenterY=-39.9996 CenterZ=0 NormalX=0 NormalY=0 NormalZ=1 AngleXU=0 Radius=5.59996 StartAngle=4.71239 EndAngle=6.28319
    g18: Circle CenterX=43.551 CenterY=-39.9996 CenterZ=0 NormalX=0 NormalY=0 NormalZ=1 AngleXU=0 Radius=2
    g19: Circle CenterX=43.5508 CenterY=33.5498 CenterZ=0 NormalX=0 NormalY=0 NormalZ=1 AngleXU=0 Radius=2
    g20: LineSegment StartX=39.5508 StartY=39.1464 StartZ=0 EndX=39.5508 EndY=33.5498 EndZ=0
    g21: ArcOfCircle CenterX=43.5508 CenterY=33.5498 CenterZ=0 NormalX=0 NormalY=0 NormalZ=1 AngleXU=0 Radius=4 StartAngle=3.14158 EndAngle=4.7124
    g22: LineSegment StartX=43.5508 StartY=29.5498 StartZ=0 EndX=49.1508 EndY=29.5498 EndZ=0
    g23: LineSegment StartX=49.1508 StartY=29.5498 StartZ=0 EndX=49.1508 EndY=33.5464 EndZ=0
    g24: ArcOfCircle CenterX=43.5508 CenterY=33.5464 CenterZ=0 NormalX=0 NormalY=0 NormalZ=1 AngleXU=0 Radius=5.59996 StartAngle=0 EndAngle=1.5708
    g25: LineSegment StartX=39.5508 StartY=39.1464 StartZ=0 EndX=43.5508 EndY=39.1464 EndZ=0
    g26: ArcOfCircle CenterX=-49.9492 CenterY=-39.9996 CenterZ=0 NormalX=0 NormalY=0 NormalZ=1 AngleXU=0 Radius=4 StartAngle=-1.8e-15 EndAngle=1.5708
    g27: LineSegment StartX=-45.9492 StartY=-39.9996 StartZ=0 EndX=-45.9492 EndY=-45.5996 EndZ=0
    g28: LineSegment StartX=39.5508 StartY=-45.5996 StartZ=0 EndX=39.5508 EndY=-39.9996 EndZ=0
    g29: ArcOfCircle CenterX=43.5508 CenterY=-39.9996 CenterZ=0 NormalX=0 NormalY=0 NormalZ=1 AngleXU=0 Radius=4 StartAngle=1.5708 EndAngle=3.14159
  constraints (74):
    c: PointOnObject(g0,g-7)
    c: Horizontal(g0)
    c: Tangent(g0,g1) = -1.5708
    c: Coincident(g1,g2)
    c: Vertical(g2)
    c: Coincident(g2,g3)
    c: Coincident(g3,g-9)
    c: Tangent(g3,g4) = -1.5708
    c: Coincident(g4,g-8)
    c: Tangent(g4,g5) = -1.5708
    c: Coincident(g6,g4)
    c: Coincident(g1,g4)
    c: DistanceY(g0,g1) = 4
    c: Coincident(g7,g-14)
    c: PointOnObject(g12,g-13)
    c: Horizontal(g8)
    c: Coincident(g9,g-14)
    c: Coincident(g9,g-7)
    c: Coincident(g8,g10)
    c: Coincident(g10,g9)
    c: Tangent(g10,g11) = -1.5708
    c: Coincident(g11,g-14)
    c: Tangent(g11,g12) = -1.5708
    c: DistanceY(g11,g8) = 4
    c: Coincident(g5,g0)
    c: Coincident(g13,g-11)
    c: Coincident(g13,g-12)
    c: Coincident(g-13,g14)
    c: PointOnObject(g14,g-13)
    c: Horizontal(g15)
    c: Coincident(g15,g16)
    c: Tangent(g16,g17) = 1.5708
    c: Coincident(g17,g14)
    c: Coincident(g16,g13)
    c: PointOnObject(g15,g13)
    c: Coincident(g21,g22)
    c: DistanceY(g21,g19) = 4
    c: DistanceX(g20,g19) = 4
    c: Coincident(g24,g23)
    c: Coincident(g23,g-11)
    c: Coincident(g24,g-10)
    c: Coincident(g24,g25)
    c: Horizontal(g25)
    c: PointOnObject(g20,g-9)
    c: Coincident(g25,g20)
    c: Coincident(g21,g-4)
    c: Horizontal(g22)
    c: PointOnObject(g22,g-11)
    c: Coincident(g22,g23)
    c: Coincident(g20,g21)
    c: Vertical(g20)
    c: Coincident(g19,g21)
    c: Vertical(g21,g24)
    c: Coincident(g18,g-5)
    c: Diameter(g6) = 4
    c: Equal(g6,g7)
    c: Equal(g6,g19)
    c: Equal(g6,g18)
    c: Horizontal(g1,g1)
    c: Coincident(g26,g8)
    c: Coincident(g27,g26)
    c: Coincident(g27,g12)
    c: Vertical(g27)
    c: DistanceX(g11,g26) = 4
    c: Coincident(g26,g11)
    c: Horizontal(g26,g7)
    c: Coincident(g28,g14)
    c: Vertical(g28)
    c: DistanceX(g28,g17) = 4
    c: Coincident(g29,g17)
    c: Coincident(g29,g28)
    c: Coincident(g29,g15)
    c: Horizontal(g17,g28)
    c: Vertical(g15,g17)
FEATURE [PartDesign::Pad] Pad005
  BaseFeature = -> Chamfer004
  Direction = (0,-1e-16,-1)
  Length = 15
  Length2 = 10
  Profile = -> Sketch015
  ReferenceAxis = -> Sketch015 [N_Axis]
  Refine = true
  Reversed = true
  SideType = 0
  Suppressed = false
  Type = 1
  Type2 = 0
FEATURE [Sketcher::SketchObject] Sketch025
  ArcFitTolerance = 1e-06
  ExternalTypes = [0]
  FullyConstrained = false
  MakeInternals = false
  MapMode = 5
  Placement = pos=(-2.8e-14,47.1996,1.079e-13) rot=(0,0.707107,0.707107;3.14159rad)
  _ExternalGeoVersion = 0
  sketch-geometry (6):
    g0: ArcOfCircle CenterX=-22.0864 CenterY=14.3686 CenterZ=0 NormalX=0 NormalY=0 NormalZ=1 AngleXU=0 Radius=1 StartAngle=5.76202 EndAngle=8.90594
    g1: ArcOfCircle CenterX=-31.0864 CenterY=-1.3502 CenterZ=0 NormalX=0 NormalY=0 NormalZ=1 AngleXU=0 Radius=0.979 StartAngle=2.62275 EndAngle=5.76202
    g2: LineSegment StartX=-21.2192 StartY=13.8707 StartZ=0 EndX=-30.2374 EndY=-1.83763 EndZ=0
    g3: LineSegment StartX=-22.9548 StartY=14.8645 StartZ=0 EndX=-31.9366 EndY=-0.864737 EndZ=0
    g4: LineSegment [constr] StartX=-31.0864 StartY=-1.3502 StartZ=0 EndX=-31.0864 EndY=-5.3502 EndZ=0
    g5: LineSegment [constr] StartX=-22.0864 StartY=14.3686 StartZ=0 EndX=-22.0864 EndY=18.6498 EndZ=0
  constraints (13):
    c: Tangent(g0,g2) = 1.5708
    c: Tangent(g0,g3) = -1.5708
    c: Tangent(g1,g2) = 1.5708
    c: Tangent(g1,g3) = -1.5708
    c: Radius(g0) = 1
    c: Coincident(g4,g1)
    c: PointOnObject(g4,g-4)
    c: Vertical(g4)
    c: DistanceX(g1,g0) = 9
    c: DistanceY(g4,g4) = 4
    c: Coincident(g5,g0)
    c: PointOnObject(g5,g-3)
    c: Vertical(g5)
FEATURE [PartDesign::Pocket] Pocket013
  BaseFeature = -> Pad005
  Direction = (-1e-16,-1,-2.4e-15)
  Length = 1.6
  Length2 = 5
  Profile = -> Sketch025
  ReferenceAxis = -> Sketch025 [N_Axis]
  Refine = true
  SideType = 0
  Suppressed = false
  Type = 2
  Type2 = 0
FEATURE [PartDesign::LinearPattern] LinearPattern
  BaseFeature = -> Pocket013
  Direction = -> Sketch025 [H_Axis]
  Direction2 = -> Sketch025 [H_Axis]
  Length = 65
  Length2 = 100
  Mode = 0
  Mode2 = 0
  Occurrences = 11
  Occurrences2 = 1
  Offset = 6.5
  Offset2 = 100
  Originals = -> [Pocket013]
  Refine = true
  Reversed2 = false
  SpacingPattern = [0]
  SpacingPattern2 = [0]
  Spacings = [-1,-1,-1,-1,-1,-1,-1,-1,-1,-1]
  Suppressed = false
  TransformMode = 0
FEATURE [Sketcher::SketchObject] Sketch028
  ArcFitTolerance = 1e-06
  AttachmentOffset = pos=(0,0,-2) rot=(0,0,1;0rad)
  AttachmentSupport = -> [Pad005]
  ExternalGeometry = -> [Pad005]
  ExternalTypes = [0,0,0,0]
  FullyConstrained = true
  MakeInternals = false
  MapMode = 5
  Placement = pos=(0,0,18.6498) rot=(1,0,0;3.14159rad)
  _ExternalGeoVersion = 1
  sketch-geometry (4):
    g0: Circle CenterX=-49.9492 CenterY=33.5464 CenterZ=0 NormalX=0 NormalY=0 NormalZ=1 AngleXU=0 Radius=2
    g1: Circle CenterX=43.5508 CenterY=33.5498 CenterZ=0 NormalX=0 NormalY=0 NormalZ=1 AngleXU=0 Radius=2
    g2: Circle CenterX=-49.9492 CenterY=-39.9996 CenterZ=0 NormalX=0 NormalY=0 NormalZ=1 AngleXU=0 Radius=2
    g3: Circle CenterX=43.551 CenterY=-39.9996 CenterZ=0 NormalX=0 NormalY=0 NormalZ=1 AngleXU=0 Radius=2
  constraints (8):
    c: Coincident(g0,g-3)
    c: Equal(g0,g-3)
    c: Coincident(g1,g-4)
    c: Equal(g1,g-4)
    c: Coincident(g2,g-6)
    c: Equal(g2,g-6)
    c: Coincident(g3,g-5)
    c: Equal(g3,g-5)
FEATURE [PartDesign::Hole] Hole
  BaseFeature = -> LinearPattern
  BaseProfileType = 7
  CustomThreadClearance = 0
  Depth = 25
  DepthType = 0
  Diameter = 3.2
  DrillForDepth = true
  DrillPoint = 1
  DrillPointAngle = 118
  HoleCutCountersinkAngle = 90
  HoleCutCustomValues = false
  HoleCutDepth = 12
  HoleCutDiameter = 6
  HoleCutType = 1
  ModelThread = false
  Profile = -> Sketch028
  Refine = true
  Reversed = true
  Suppressed = false
  Tapered = false
  TaperedAngle = 90
  ThreadClass = 0
  ThreadDepth = 25
  ThreadDepthType = 0
  ThreadDiameter = 3.2
  ThreadDirection = 0
  ThreadFit = 0
  ThreadSize = 0
  ThreadType = 0
  Threaded = false
  UseCustomThreadClearance = false
FEATURE [Sketcher::SketchObject] Sketch027
  ArcFitTolerance = 1e-06
  ExternalGeometry = -> [Hole]
  ExternalTypes = [0]
  FullyConstrained = false
  MakeInternals = false
  MapMode = 5
  Placement = pos=(0,-40.7464,7.21e-14) rot=(1,0,0;1.5708rad)
  _ExternalGeoVersion = 1
  sketch-geometry (5):
    g0: LineSegment StartX=4.44763 StartY=1.6498 StartZ=0 EndX=4.44763 EndY=15.1498 EndZ=0
    g1: LineSegment StartX=4.44763 StartY=15.1498 StartZ=0 EndX=32.4476 EndY=15.1498 EndZ=0
    g2: LineSegment StartX=32.4476 StartY=15.1498 StartZ=0 EndX=32.4476 EndY=1.6498 EndZ=0
    g3: LineSegment StartX=4.44763 StartY=1.6498 StartZ=0 EndX=32.4476 EndY=1.6498 EndZ=0
    g4: LineSegment [constr] StartX=32.4476 StartY=15.1498 StartZ=0 EndX=32.4476 EndY=16.6498 EndZ=0
  constraints (14):
    c: Vertical(g2)
    c: Vertical(g0)
    c: Coincident(g1,g2)
    c: Coincident(g0,g1)
    c: DistanceX(g0,g2) = 28
    c: Horizontal(g3)
    c: Coincident(g3,g0)
    c: Coincident(g3,g2)
    c: DistanceY(g2,g2) = 13.5
    c: Horizontal(g1)
    c: Coincident(g4,g1)
    c: PointOnObject(g4,g-3)
    c: Vertical(g4)
    c: DistanceY(g4,g4) = 1.5
FEATURE [PartDesign::Pocket] Pocket014
  BaseFeature = -> Hole
  Direction = (0,1,-1.8e-15)
  Length = 9.5
  Length2 = 5
  Profile = -> Sketch027
  ReferenceAxis = -> Sketch027 [N_Axis]
  Refine = true
  SideType = 0
  Suppressed = false
  Type = 0
  Type2 = 0
FEATURE [Sketcher::SketchObject] Sketch029
  ArcFitTolerance = 1e-06
  AttachmentOffset = pos=(0,0,22) rot=(0,0,1;0rad)
  AttachmentSupport = -> [XY_Plane033]
  ExternalTypes = [0]
  FullyConstrained = false
  MakeInternals = false
  MapMode = 5
  Placement = pos=(0,0,22) rot=(0,0,1;0rad)
  _ExternalGeoVersion = 1
  sketch-geometry (10):
    g0: Circle CenterX=-50.4765 CenterY=16.1316 CenterZ=0 NormalX=0 NormalY=0 NormalZ=1 AngleXU=0 Radius=1.875
    g1: Circle CenterX=-50.4765 CenterY=-9.6684 CenterZ=0 NormalX=0 NormalY=0 NormalZ=1 AngleXU=0 Radius=1.875
    g2: Circle CenterX=-24.6765 CenterY=-9.6684 CenterZ=0 NormalX=0 NormalY=0 NormalZ=1 AngleXU=0 Radius=1.875
    g3: Circle CenterX=-24.6765 CenterY=16.1316 CenterZ=0 NormalX=0 NormalY=0 NormalZ=1 AngleXU=0 Radius=1.875
    g4: LineSegment [constr] StartX=-50.4765 StartY=16.1316 StartZ=0 EndX=-50.4765 EndY=-9.6684 EndZ=0
    g5: LineSegment [constr] StartX=-50.4765 StartY=-9.6684 StartZ=0 EndX=-24.6765 EndY=-9.6684 EndZ=0
    g6: LineSegment [constr] StartX=-24.6765 StartY=-9.6684 StartZ=0 EndX=-24.6765 EndY=16.1316 EndZ=0
    g7: LineSegment [constr] StartX=-24.6765 StartY=16.1316 StartZ=0 EndX=-50.4765 EndY=16.1316 EndZ=0
    g8: LineSegment [constr] StartX=-50.4765 StartY=-9.6684 StartZ=0 EndX=0 EndY=1.5666 EndZ=0
    g9: LineSegment [constr] StartX=9e-16 StartY=4.8966 StartZ=0 EndX=-50.4765 EndY=16.1316 EndZ=0
  constraints (23):
    c: Diameter(g0) = 3.75
    c: Coincident(g4,g5)
    c: Coincident(g5,g6)
    c: Coincident(g6,g7)
    c: Coincident(g7,g4)
    c: Vertical(g4)
    c: Vertical(g6)
    c: Horizontal(g5)
    c: Horizontal(g7)
    c: Coincident(g4,g0)
    c: Coincident(g5,g2)
    c: Equal(g4,g7)
    c: DistanceY(g4,g4) = 25.8
    c: Coincident(g4,g1)
    c: Coincident(g6,g3)
    c: Equal(g0,g3)
    c: Equal(g0,g2)
    c: Equal(g0,g1)
    c: Coincident(g8,g1)
    c: Coincident(g8,g-3)
    c: Coincident(g9,g-3)
    c: Coincident(g9,g0)
    c: Equal(g8,g9)
FEATURE [Sketcher::SketchObject] Sketch030
  ArcFitTolerance = 1e-06
  AttachmentOffset = pos=(-43,-4,0) rot=(0,0,1;0rad)
  AttachmentSupport = -> [Pad004]
  ExternalTypes = [0]
  FullyConstrained = false
  MakeInternals = false
  MapMode = 5
  Placement = pos=(-43,4,16.6498) rot=(1,0,0;3.14159rad)
  _ExternalGeoVersion = 1
  sketch-geometry (84):
    g0: LineSegment StartX=-0.997308 StartY=-8.92815 StartZ=0 EndX=-4.46141 EndY=-10.9281 EndZ=0
    g1: LineSegment StartX=-4.46141 StartY=-10.9281 StartZ=0 EndX=-4.46141 EndY=-14.9281 EndZ=0
    g2: LineSegment StartX=-4.46141 StartY=-14.9281 StartZ=0 EndX=-0.997308 EndY=-16.9281 EndZ=0
    g3: LineSegment StartX=-0.997308 StartY=-16.9281 StartZ=0 EndX=2.46679 EndY=-14.9281 EndZ=0
    g4: LineSegment StartX=2.46679 StartY=-14.9281 StartZ=0 EndX=2.46679 EndY=-10.9281 EndZ=0
    g5: LineSegment StartX=2.46679 StartY=-10.9281 StartZ=0 EndX=-0.997308 EndY=-8.92815 EndZ=0
    g6: Circle [constr] CenterX=-0.997308 CenterY=-12.9281 CenterZ=0 NormalX=0 NormalY=0 NormalZ=1 AngleXU=0 Radius=4
    g7: LineSegment StartX=-4.96141 StartY=-2.06212 StartZ=0 EndX=-8.42551 EndY=-4.06212 EndZ=0
    g8: LineSegment StartX=-8.42551 StartY=-4.06212 StartZ=0 EndX=-8.42551 EndY=-8.06212 EndZ=0
    g9: LineSegment StartX=-8.42551 StartY=-8.06212 StartZ=0 EndX=-4.96141 EndY=-10.0621 EndZ=0
    g10: LineSegment StartX=-4.96141 StartY=-10.0621 StartZ=0 EndX=-1.49731 EndY=-8.06212 EndZ=0
    g11: LineSegment StartX=-1.49731 StartY=-8.06212 StartZ=0 EndX=-1.49731 EndY=-4.06212 EndZ=0
    g12: LineSegment StartX=-1.49731 StartY=-4.06212 StartZ=0 EndX=-4.96141 EndY=-2.06212 EndZ=0
    g13: Circle [constr] CenterX=-4.96141 CenterY=-6.06212 CenterZ=0 NormalX=0 NormalY=0 NormalZ=1 AngleXU=0 Radius=4
    g14: LineSegment [constr] StartX=-1.49731 StartY=-8.06212 StartZ=0 EndX=-0.497308 EndY=-8.06212 EndZ=0
    g15: LineSegment [constr] StartX=-0.497308 StartY=-8.06212 StartZ=0 EndX=-0.997308 EndY=-8.92815 EndZ=0
    g16: LineSegment [constr] StartX=-0.997308 StartY=-8.92815 StartZ=0 EndX=-1.49731 EndY=-8.06212 EndZ=0
    g17: Circle [constr] CenterX=6.93089 CenterY=-12.9281 CenterZ=0 NormalX=0 NormalY=0 NormalZ=1 AngleXU=0 Radius=4
    g18: LineSegment StartX=3.46679 StartY=-10.9281 StartZ=0 EndX=3.46679 EndY=-14.9281 EndZ=0
    g19: LineSegment StartX=6.93089 StartY=-8.92815 StartZ=0 EndX=3.46679 EndY=-10.9281 EndZ=0
    g20: LineSegment StartX=10.395 StartY=-10.9281 StartZ=0 EndX=6.93089 EndY=-8.92815 EndZ=0
    g21: LineSegment StartX=10.395 StartY=-14.9281 StartZ=0 EndX=10.395 EndY=-10.9281 EndZ=0
    g22: LineSegment StartX=6.93089 StartY=-16.9281 StartZ=0 EndX=10.395 EndY=-14.9281 EndZ=0
    g23: LineSegment StartX=3.46679 StartY=-14.9281 StartZ=0 EndX=6.93089 EndY=-16.9281 EndZ=0
    g24: LineSegment StartX=2.96679 StartY=-2.06212 StartZ=0 EndX=-0.497308 EndY=-4.06212 EndZ=0
    g25: LineSegment StartX=-0.497308 StartY=-4.06212 StartZ=0 EndX=-0.497308 EndY=-8.06212 EndZ=0
    g26: LineSegment StartX=-0.497308 StartY=-8.06212 StartZ=0 EndX=2.96679 EndY=-10.0621 EndZ=0
    g27: LineSegment StartX=2.96679 StartY=-10.0621 StartZ=0 EndX=6.43089 EndY=-8.06212 EndZ=0
    g28: LineSegment StartX=6.43089 StartY=-8.06212 StartZ=0 EndX=6.43089 EndY=-4.06212 EndZ=0
    g29: LineSegment StartX=6.43089 StartY=-4.06212 StartZ=0 EndX=2.96679 EndY=-2.06212 EndZ=0
    g30: Circle [constr] CenterX=2.96679 CenterY=-6.06212 CenterZ=0 NormalX=0 NormalY=0 NormalZ=1 AngleXU=0 Radius=4
    g31: LineSegment [constr] StartX=6.43089 StartY=-8.06212 StartZ=0 EndX=7.43089 EndY=-8.06212 EndZ=0
    g32: LineSegment [constr] StartX=7.43089 StartY=-8.06212 StartZ=0 EndX=6.93089 EndY=-8.92815 EndZ=0
    g33: LineSegment [constr] StartX=6.93089 StartY=-8.92815 StartZ=0 EndX=6.43089 EndY=-8.06212 EndZ=0
    g34: LineSegment StartX=10.895 StartY=-2.06212 StartZ=0 EndX=7.43089 EndY=-4.06212 EndZ=0
    g35: LineSegment StartX=7.43089 StartY=-4.06212 StartZ=0 EndX=7.43089 EndY=-8.06212 EndZ=0
    g36: LineSegment StartX=7.43089 StartY=-8.06212 StartZ=0 EndX=10.895 EndY=-10.0621 EndZ=0
    g37: LineSegment StartX=10.895 StartY=-10.0621 StartZ=0 EndX=14.3591 EndY=-8.06212 EndZ=0
    g38: LineSegment StartX=14.3591 StartY=-8.06212 StartZ=0 EndX=14.3591 EndY=-4.06212 EndZ=0
    g39: LineSegment StartX=14.3591 StartY=-4.06212 StartZ=0 EndX=10.895 EndY=-2.06212 EndZ=0
    g40: Circle [constr] CenterX=10.895 CenterY=-6.06212 CenterZ=0 NormalX=0 NormalY=0 NormalZ=1 AngleXU=0 Radius=4
    g41: LineSegment StartX=6.93089 StartY=8.92815 StartZ=0 EndX=10.395 EndY=10.9281 EndZ=0
    g42: LineSegment StartX=10.395 StartY=10.9281 StartZ=0 EndX=10.395 EndY=14.9281 EndZ=0
    g43: LineSegment StartX=10.395 StartY=14.9281 StartZ=0 EndX=6.93089 EndY=16.9281 EndZ=0
    g44: LineSegment StartX=6.93089 StartY=16.9281 StartZ=0 EndX=3.46679 EndY=14.9281 EndZ=0
    g45: LineSegment StartX=3.46679 StartY=14.9281 StartZ=0 EndX=3.46679 EndY=10.9281 EndZ=0
    g46: LineSegment StartX=3.46679 StartY=10.9281 StartZ=0 EndX=6.93089 EndY=8.92815 EndZ=0
    g47: Circle [constr] CenterX=6.93089 CenterY=12.9281 CenterZ=0 NormalX=0 NormalY=0 NormalZ=1 AngleXU=0 Radius=4
    g48: LineSegment StartX=10.895 StartY=2.06212 StartZ=0 EndX=14.3591 EndY=4.06212 EndZ=0
    g49: LineSegment StartX=14.3591 StartY=4.06212 StartZ=0 EndX=14.3591 EndY=8.06212 EndZ=0
    g50: LineSegment StartX=14.3591 StartY=8.06212 StartZ=0 EndX=10.895 EndY=10.0621 EndZ=0
    g51: LineSegment StartX=10.895 StartY=10.0621 StartZ=0 EndX=7.43089 EndY=8.06212 EndZ=0
    g52: LineSegment StartX=7.43089 StartY=8.06212 StartZ=0 EndX=7.43089 EndY=4.06212 EndZ=0
    g53: LineSegment StartX=7.43089 StartY=4.06212 StartZ=0 EndX=10.895 EndY=2.06212 EndZ=0
    g54: Circle [constr] CenterX=10.895 CenterY=6.06212 CenterZ=0 NormalX=0 NormalY=0 NormalZ=1 AngleXU=0 Radius=4
    g55: LineSegment [constr] StartX=7.43089 StartY=8.06212 StartZ=0 EndX=6.43089 EndY=8.06212 EndZ=0
    g56: LineSegment [constr] StartX=6.43089 StartY=8.06212 StartZ=0 EndX=6.93089 EndY=8.92815 EndZ=0
    g57: LineSegment [constr] StartX=6.93089 StartY=8.92815 StartZ=0 EndX=7.43089 EndY=8.06212 EndZ=0
    g58: Circle [constr] CenterX=-0.997308 CenterY=12.9281 CenterZ=0 NormalX=0 NormalY=0 NormalZ=1 AngleXU=0 Radius=4
    g59: LineSegment StartX=2.46679 StartY=10.9281 StartZ=0 EndX=2.46679 EndY=14.9281 EndZ=0
    g60: LineSegment StartX=-0.997308 StartY=8.92815 StartZ=0 EndX=2.46679 EndY=10.9281 EndZ=0
    g61: LineSegment StartX=-4.46141 StartY=10.9281 StartZ=0 EndX=-0.997308 EndY=8.92815 EndZ=0
    g62: LineSegment StartX=-4.46141 StartY=14.9281 StartZ=0 EndX=-4.46141 EndY=10.9281 EndZ=0
    g63: LineSegment StartX=-0.997308 StartY=16.9281 StartZ=0 EndX=-4.46141 EndY=14.9281 EndZ=0
    g64: LineSegment StartX=2.46679 StartY=14.9281 StartZ=0 EndX=-0.997308 EndY=16.9281 EndZ=0
    g65: LineSegment StartX=2.96679 StartY=2.06212 StartZ=0 EndX=6.43089 EndY=4.06212 EndZ=0
    g66: LineSegment StartX=6.43089 StartY=4.06212 StartZ=0 EndX=6.43089 EndY=8.06212 EndZ=0
    g67: LineSegment StartX=6.43089 StartY=8.06212 StartZ=0 EndX=2.96679 EndY=10.0621 EndZ=0
    g68: LineSegment StartX=2.96679 StartY=10.0621 StartZ=0 EndX=-0.497308 EndY=8.06212 EndZ=0
    g69: LineSegment StartX=-0.497308 StartY=8.06212 StartZ=0 EndX=-0.497308 EndY=4.06212 EndZ=0
    g70: LineSegment StartX=-0.497308 StartY=4.06212 StartZ=0 EndX=2.96679 EndY=2.06212 EndZ=0
    g71: Circle [constr] CenterX=2.96679 CenterY=6.06212 CenterZ=0 NormalX=0 NormalY=0 NormalZ=1 AngleXU=0 Radius=4
    g72: LineSegment [constr] StartX=-0.497308 StartY=8.06212 StartZ=0 EndX=-1.49731 EndY=8.06212 EndZ=0
    g73: LineSegment [constr] StartX=-1.49731 StartY=8.06212 StartZ=0 EndX=-0.997308 EndY=8.92815 EndZ=0
    g74: LineSegment [constr] StartX=-0.997308 StartY=8.92815 StartZ=0 EndX=-0.497308 EndY=8.06212 EndZ=0
    g75: LineSegment StartX=-4.96141 StartY=2.06212 StartZ=0 EndX=-1.49731 EndY=4.06212 EndZ=0
    g76: LineSegment StartX=-1.49731 StartY=4.06212 StartZ=0 EndX=-1.49731 EndY=8.06212 EndZ=0
    g77: LineSegment StartX=-1.49731 StartY=8.06212 StartZ=0 EndX=-4.96141 EndY=10.0621 EndZ=0
    g78: LineSegment StartX=-4.96141 StartY=10.0621 StartZ=0 EndX=-8.42551 EndY=8.06212 EndZ=0
    g79: LineSegment StartX=-8.42551 StartY=8.06212 StartZ=0 EndX=-8.42551 EndY=4.06212 EndZ=0
    g80: LineSegment StartX=-8.42551 StartY=4.06212 StartZ=0 EndX=-4.96141 EndY=2.06212 EndZ=0
    g81: Circle [constr] CenterX=-4.96141 CenterY=6.06212 CenterZ=0 NormalX=0 NormalY=0 NormalZ=1 AngleXU=0 Radius=4
    g82: LineSegment [constr] StartX=-4.96141 StartY=2.06212 StartZ=0 EndX=0 EndY=0 EndZ=0
    g83: LineSegment [constr] StartX=0 StartY=0 StartZ=0 EndX=-4.96141 EndY=-2.06212 EndZ=0
  constraints (220):
    c: Coincident(g0,g1)
    c: Coincident(g1,g2)
    c: Coincident(g2,g3)
    c: Coincident(g3,g4)
    c: Coincident(g4,g5)
    c: Coincident(g5,g0)
    c: Equal(g0, g1-g5) x5
    c: PointOnObject(g0,g6)
    c: PointOnObject(g1,g6)
    c: PointOnObject(g2,g6)
    c: PointOnObject(g3,g6)
    c: PointOnObject(g4,g6)
    c: PointOnObject(g5,g6)
    c: Radius(g6) = 4
    c: Coincident(g7,g8)
    c: Coincident(g8,g9)
    c: Coincident(g9,g10)
    c: Coincident(g10,g11)
    c: Coincident(g11,g12)
    c: Coincident(g12,g7)
    c: Equal(g7, g8-g12) x5
    c: PointOnObject(g7,g13)
    c: PointOnObject(g8,g13)
    c: PointOnObject(g9,g13)
    c: PointOnObject(g10,g13)
    c: PointOnObject(g11,g13)
    c: PointOnObject(g12,g13)
    c: Radius(g13) = 4
    c: Coincident(g10,g14)
    c: Coincident(g14,g15)
    c: Coincident(g15,g0)
    c: Coincident(g15,g16)
    c: Coincident(g16,g14)
    c: Equal(g14,g15)
    c: Equal(g14,g16)
    c: Horizontal(g14)
    c: Vertical(g11)
    c: Vertical(g1)
    c: Distance(g0,g10) = 1
    c: Coincident(g19,g18)
    c: Coincident(g18,g23)
    c: Coincident(g23,g22)
    c: Coincident(g22,g21)
    c: Coincident(g21,g20)
    c: Coincident(g20,g19)
    c: Equal(g19,g18)
    c: Equal(g19,g23)
    c: Equal(g19,g22)
    c: Equal(g19,g21)
    c: Equal(g19,g20)
    c: PointOnObject(g19,g17)
    c: PointOnObject(g18,g17)
    c: PointOnObject(g23,g17)
    c: PointOnObject(g22,g17)
    c: PointOnObject(g21,g17)
    c: PointOnObject(g20,g17)
    c: Radius(g17) = 4
    c: Coincident(g24,g25)
    c: Coincident(g34,g35)
    c: Coincident(g25,g26)
    c: Coincident(g35,g36)
    c: Coincident(g26,g27)
    c: Coincident(g36,g37)
    c: Coincident(g27,g28)
    c: Coincident(g37,g38)
    c: Coincident(g28,g29)
    c: Coincident(g38,g39)
    c: Coincident(g29,g24)
    c: Coincident(g39,g34)
    c: Equal(g24,g25)
    c: Equal(g34,g35)
    c: Equal(g24,g26)
    c: Equal(g34,g36)
    c: Equal(g24,g27)
    c: Equal(g34,g37)
    c: Equal(g24,g28)
    c: Equal(g34,g38)
    c: Equal(g24,g29)
    c: Equal(g34,g39)
    c: PointOnObject(g24,g30)
    c: PointOnObject(g34,g40)
    c: PointOnObject(g25,g30)
    c: PointOnObject(g35,g40)
    c: PointOnObject(g26,g30)
    c: PointOnObject(g36,g40)
    c: PointOnObject(g27,g30)
    c: PointOnObject(g37,g40)
    c: PointOnObject(g28,g30)
    c: PointOnObject(g38,g40)
    c: PointOnObject(g29,g30)
    c: PointOnObject(g39,g40)
    c: Radius(g30) = 4
    c: Radius(g40) = 4
    c: Coincident(g27,g31)
    c: Coincident(g31,g32)
    c: Coincident(g32,g19)
    c: Coincident(g32,g33)
    c: Coincident(g33,g31)
    c: Equal(g31,g32)
    c: Equal(g31,g33)
    c: Horizontal(g31)
    c: Vertical(g28)
    c: Vertical(g38)
    c: Vertical(g18)
    c: Distance(g19,g27) = 1
    c: Coincident(g25,g14)
    c: Coincident(g31,g35)
    c: Coincident(g41,g42)
    c: Coincident(g42,g43)
    c: Coincident(g43,g44)
    c: Coincident(g44,g45)
    c: Coincident(g45,g46)
    c: Coincident(g46,g41)
    c: Equal(g41, g42-g46) x5
    c: PointOnObject(g41,g47)
    c: PointOnObject(g42,g47)
    c: PointOnObject(g43,g47)
    c: PointOnObject(g44,g47)
    c: PointOnObject(g45,g47)
    c: PointOnObject(g46,g47)
    c: Radius(g47) = 4
    c: Coincident(g48,g49)
    c: Coincident(g49,g50)
    c: Coincident(g50,g51)
    c: Coincident(g51,g52)
    c: Coincident(g52,g53)
    c: Coincident(g53,g48)
    c: Equal(g48, g49-g53) x5
    c: PointOnObject(g48,g54)
    c: PointOnObject(g49,g54)
    c: PointOnObject(g50,g54)
    c: PointOnObject(g51,g54)
    c: PointOnObject(g52,g54)
    c: PointOnObject(g53,g54)
    c: Radius(g54) = 4
    c: Coincident(g51,g55)
    c: Coincident(g55,g56)
    c: Coincident(g56,g41)
    c: Coincident(g56,g57)
    c: Coincident(g57,g55)
    c: Equal(g55,g56)
    c: Equal(g55,g57)
    c: Horizontal(g55)
    c: Vertical(g52)
    c: Vertical(g42)
    c: Distance(g41,g51) = 1
    c: Coincident(g60,g59)
    c: Coincident(g59,g64)
    c: Coincident(g64,g63)
    c: Coincident(g63,g62)
    c: Coincident(g62,g61)
    c: Coincident(g61,g60)
    c: Equal(g60,g59)
    c: Equal(g60,g64)
    c: Equal(g60,g63)
    c: Equal(g60,g62)
    c: Equal(g60,g61)
    c: PointOnObject(g60,g58)
    c: PointOnObject(g59,g58)
    c: PointOnObject(g64,g58)
    c: PointOnObject(g63,g58)
    c: PointOnObject(g62,g58)
    c: PointOnObject(g61,g58)
    c: Radius(g58) = 4
    c: Coincident(g65,g66)
    c: Coincident(g75,g76)
    c: Coincident(g66,g67)
    c: Coincident(g76,g77)
    c: Coincident(g67,g68)
    c: Coincident(g77,g78)
    c: Coincident(g68,g69)
    c: Coincident(g78,g79)
    c: Coincident(g69,g70)
    c: Coincident(g79,g80)
    c: Coincident(g70,g65)
    c: Coincident(g80,g75)
    c: Equal(g65,g66)
    c: Equal(g75,g76)
    c: Equal(g65,g67)
    c: Equal(g75,g77)
    c: Equal(g65,g68)
    c: Equal(g75,g78)
    c: Equal(g65,g69)
    c: Equal(g75,g79)
    c: Equal(g65,g70)
    c: Equal(g75,g80)
    c: PointOnObject(g65,g71)
    c: PointOnObject(g75,g81)
    c: PointOnObject(g66,g71)
    c: PointOnObject(g76,g81)
    c: PointOnObject(g67,g71)
    c: PointOnObject(g77,g81)
    c: PointOnObject(g68,g71)
    c: PointOnObject(g78,g81)
    c: PointOnObject(g69,g71)
    c: PointOnObject(g79,g81)
    c: PointOnObject(g70,g71)
    c: PointOnObject(g80,g81)
    c: Radius(g71) = 4
    c: Radius(g81) = 4
    c: Coincident(g68,g72)
    c: Coincident(g72,g73)
    c: Coincident(g73,g60)
    c: Coincident(g73,g74)
    c: Coincident(g74,g72)
    c: Equal(g72,g73)
    c: Equal(g72,g74)
    c: Horizontal(g72)
    c: Vertical(g69)
    c: Vertical(g79)
    c: Vertical(g59)
    c: Distance(g60,g68) = 1
    c: Coincident(g66,g55)
    c: Coincident(g72,g76)
    c: Coincident(g82,g75)
    c: Coincident(g82,g-1)
    c: Coincident(g83,g82)
    c: Coincident(g83,g7)
    c: Equal(g82,g83)
    c: Vertical(g7,g75)
FEATURE [Sketcher::SketchObject] Sketch031
  ArcFitTolerance = 1e-06
  ExternalTypes = [0]
  FullyConstrained = false
  MakeInternals = false
  MapMode = 5
  Placement = pos=(0,0,18.6498) rot=(0,0,1;0rad)
  _ExternalGeoVersion = 1
  sketch-geometry (6):
    g0: LineSegment StartX=-57.1492 StartY=32.4113 StartZ=0 EndX=16.7268 EndY=32.4113 EndZ=0
    g1: LineSegment StartX=16.7268 StartY=32.4113 StartZ=0 EndX=16.7268 EndY=-25.9581 EndZ=0
    g2: LineSegment StartX=16.7268 StartY=-25.9581 StartZ=0 EndX=-57.1492 EndY=-25.9581 EndZ=0
    g3: LineSegment StartX=-57.1492 StartY=-25.9581 StartZ=0 EndX=-57.1492 EndY=32.4113 EndZ=0
    g4: LineSegment [constr] StartX=-57.1492 StartY=39.9996 StartZ=0 EndX=-57.1492 EndY=32.4113 EndZ=0
    g5: LineSegment [constr] StartX=-57.1492 StartY=-25.9581 StartZ=0 EndX=-57.1492 EndY=-33.5464 EndZ=0
  constraints (14):
    c: PointOnObject(g0,g-3)
    c: Horizontal(g0)
    c: Coincident(g0,g1)
    c: Vertical(g1)
    c: Coincident(g1,g2)
    c: PointOnObject(g2,g-3)
    c: Horizontal(g2)
    c: Coincident(g2,g3)
    c: Coincident(g3,g0)
    c: Coincident(g4,g-3)
    c: Coincident(g4,g0)
    c: Coincident(g5,g2)
    c: Coincident(g5,g-3)
    c: Equal(g4,g5)
FEATURE [PartDesign::Pad] Pad013
  BaseFeature = -> Pocket014
  Direction = (0,0,1)
  Length = 12
  Length2 = 10
  Profile = -> Sketch031
  ReferenceAxis = -> Sketch031 [N_Axis]
  Refine = true
  SideType = 0
  Suppressed = false
  Type = 0
  Type2 = 0
FEATURE [Sketcher::SketchObject] Sketch032
  ArcFitTolerance = 1e-06
  AttachmentSupport = -> [Pad013]
  ExternalGeometry = -> [Pad013]
  ExternalTypes = [0,0]
  FullyConstrained = false
  MakeInternals = false
  MapMode = 5
  Placement = pos=(0,-25.9581,0) rot=(1,0,0;1.5708rad)
  _ExternalGeoVersion = 1
  sketch-geometry (3):
    g0: LineSegment StartX=16.7268 StartY=18.6498 StartZ=0 EndX=-31.092 EndY=30.6498 EndZ=0
    g1: LineSegment StartX=-31.092 StartY=30.6498 StartZ=0 EndX=16.7268 EndY=30.6498 EndZ=0
    g2: LineSegment StartX=16.7268 StartY=30.6498 StartZ=0 EndX=16.7268 EndY=18.6498 EndZ=0
  constraints (6):
    c: Coincident(g0,g-3)
    c: PointOnObject(g0,g-4)
    c: Coincident(g0,g1)
    c: Coincident(g1,g-4)
    c: Coincident(g1,g2)
    c: Coincident(g2,g0)
FEATURE [PartDesign::Pocket] Pocket016
  BaseFeature = -> Pad013
  Direction = (0,1,-2e-16)
  Length = 5
  Length2 = 5
  Profile = -> Sketch032
  ReferenceAxis = -> Sketch032 [N_Axis]
  Refine = true
  SideType = 0
  Suppressed = false
  Type = 2
  Type2 = 0
FEATURE [Sketcher::SketchObject] Sketch034
  ArcFitTolerance = 1e-06
  AttachmentOffset = pos=(0,-9.25,-40) rot=(0,0,1;0rad)
  AttachmentSupport = -> [Pocket016]
  ExternalTypes = [0,0]
  FullyConstrained = false
  MakeInternals = false
  MapMode = 5
  Placement = pos=(-17.1492,3.41e-14,-9.25) rot=(0.57735,-0.57735,-0.57735;2.0944rad)
  _ExternalGeoVersion = 1
  sketch-geometry (14):
    g0: LineSegment StartX=1.81444 StartY=34.2498 StartZ=0 EndX=-8.18556 EndY=34.2498 EndZ=0
    g1: LineSegment StartX=-8.18556 StartY=34.2498 StartZ=0 EndX=-8.18556 EndY=48.2498 EndZ=0
    g2: LineSegment StartX=-8.18556 StartY=105.25 StartZ=0 EndX=1.81444 EndY=105.25 EndZ=0
    g3: LineSegment StartX=1.81444 StartY=105.25 StartZ=0 EndX=1.81444 EndY=83.9585 EndZ=0
    g4: LineSegment StartX=1.81444 StartY=83.9585 StartZ=0 EndX=14.6044 EndY=53.8327 EndZ=0
    g5: LineSegment StartX=14.6044 StartY=48.2498 StartZ=0 EndX=1.81444 EndY=48.2498 EndZ=0
    g6: LineSegment StartX=-20.9755 StartY=53.8327 StartZ=0 EndX=-8.18556 EndY=83.9585 EndZ=0
    g7: LineSegment StartX=-8.18556 StartY=48.2498 StartZ=0 EndX=-20.9755 EndY=48.2498 EndZ=0
    g8: LineSegment StartX=1.81444 StartY=48.2498 StartZ=0 EndX=1.81444 EndY=34.2498 EndZ=0
    g9: LineSegment StartX=-8.18556 StartY=83.9585 StartZ=0 EndX=-8.18556 EndY=105.25 EndZ=0
    g10: GeomPoint [constr] X=1.81444 Y=105.25 Z=0
    g11: GeomPoint [constr] X=-8.18556 Y=105.25 Z=0
    g12: LineSegment StartX=-20.9755 StartY=53.8327 StartZ=0 EndX=-20.9755 EndY=48.2498 EndZ=0
    g13: LineSegment StartX=14.6044 StartY=48.2498 StartZ=0 EndX=14.6044 EndY=53.8327 EndZ=0
  constraints (33):
    c: Coincident(g0,g1)
    c: Coincident(g8,g0)
    c: DistanceX(g0,g0) = 10
    c: Horizontal(g0)
    c: Horizontal(g2)
    c: Horizontal(g5)
    c: Horizontal(g7)
    c: Vertical(g3)
    c: Vertical(g8)
    c: Coincident(g5,g8)
    c: Coincident(g3,g4)
    c: Coincident(g7,g1)
    c: Vertical(g1)
    c: Horizontal(g1,g5)
    c: Distance(g11,g7) = 57
    c: Coincident(g6,g9)
    c: Horizontal(g6,g3)
    c: Vertical(g6,g1)
    c: Vertical(g3,g5)
    c: Equal(g7,g5)
    c: Equal(g4,g6)
    c: Coincident(g12,g6)
    c: Coincident(g12,g7)
    c: Coincident(g13,g5)
    c: Coincident(g13,g4)
    c: Equal(g12,g13)
    c: Vertical(g12)
    c: Coincident(g2,g11)
    c: Coincident(g2,g9)
    c: Vertical(g9)
    c: Coincident(g2,g10)
    c: Coincident(g3,g2)
    c: DistanceY(g1,g1) = 14
FEATURE [PartDesign::Pad] Pad014
  BaseFeature = -> Pocket016
  Direction = (-1,1e-16,3.2e-15)
  Length = 3
  Length2 = 10
  Profile = -> Sketch034
  ReferenceAxis = -> Sketch034 [N_Axis]
  Refine = true
  Reversed = true
  SideType = 0
  Suppressed = false
  Type = 0
  Type2 = 0
FEATURE [Sketcher::SketchObject] Sketch035
  ArcFitTolerance = 1e-06
  AttachmentOffset = pos=(0,0,-3.33) rot=(0,0,1;0rad)
  AttachmentSupport = -> [Pad014]
  ExternalGeometry = -> [Pad014]
  ExternalTypes = [0,0,0,0]
  FullyConstrained = false
  MakeInternals = false
  MapMode = 5
  Placement = pos=(9e-16,4.85556,1.6e-15) rot=(0,0.707107,0.707107;3.14159rad)
  _ExternalGeoVersion = 1
  sketch-geometry (10):
    g0: LineSegment StartX=-32.2465 StartY=18.2979 StartZ=0 EndX=14.1492 EndY=18.2979 EndZ=0
    g1: LineSegment StartX=8.14919 StartY=95.9998 StartZ=0 EndX=-32.2465 EndY=18.2979 EndZ=0
    g2: LineSegment StartX=-18.8279 StartY=33.2691 StartZ=0 EndX=5.71451 EndY=80.477 EndZ=0
    g3: ArcOfCircle CenterX=7.47055 CenterY=79.5641 CenterZ=0 NormalX=0 NormalY=0 NormalZ=1 AngleXU=0 Radius=1.97917 StartAngle=2.4e-15 EndAngle=2.66217
    g4: LineSegment StartX=9.44972 StartY=79.5641 StartZ=0 EndX=9.44972 EndY=32.3562 EndZ=0
    g5: ArcOfCircle CenterX=7.47055 CenterY=32.3562 CenterZ=0 NormalX=0 NormalY=0 NormalZ=1 AngleXU=0 Radius=1.97917 StartAngle=4.71239 EndAngle=6.28319
    g6: LineSegment StartX=7.47055 StartY=30.377 StartZ=0 EndX=-17.0719 EndY=30.377 EndZ=0
    g7: ArcOfCircle CenterX=-17.0719 CenterY=32.3562 CenterZ=0 NormalX=0 NormalY=0 NormalZ=1 AngleXU=0 Radius=1.97917 StartAngle=2.66217 EndAngle=4.71239
    g8: LineSegment StartX=14.1492 StartY=95.9998 StartZ=0 EndX=8.14919 EndY=95.9998 EndZ=0
    g9: LineSegment StartX=14.1492 StartY=95.9998 StartZ=0 EndX=14.1492 EndY=18.2979 EndZ=0
  constraints (21):
    c: Coincident(g1,g0)
    c: Tangent(g2,g3) = 1.5708
    c: Vertical(g4)
    c: Tangent(g4,g5) = 1.5708
    c: Tangent(g6,g7) = 1.5708
    c: Parallel(g2,g1)
    c: Distance(g1,g2) = 5
    c: Distance(g8) = 6
    c: Horizontal(g8)
    c: Coincident(g1,g8)
    c: Tangent(g3,g4) = 1.5708
    c: Equal(g7,g5)
    c: Equal(g7,g3)
    c: Horizontal(g6)
    c: Tangent(g7,g2) = 1.5708
    c: Tangent(g5,g6) = 1.5708
    c: Coincident(g8,g-3)
    c: Coincident(g9,g8)
    c: Coincident(g9,g0)
    c: Vertical(g9)
    c: Horizontal(g0)
FEATURE [PartDesign::Pad] Pad015
  BaseFeature = -> Pad014
  Direction = (0,1,-2e-16)
  Length = 3.33
  Length2 = 10
  Profile = -> Sketch035
  ReferenceAxis = -> Sketch035 [N_Axis]
  Refine = true
  Reversed = true
  SideType = 0
  Suppressed = false
  Type = 0
  Type2 = 0
FEATURE [Sketcher::SketchObject] Sketch036
  ArcFitTolerance = 1e-06
  AttachmentSupport = -> [Pad015]
  ExternalGeometry = -> [Pad015]
  ExternalTypes = [0]
  FullyConstrained = false
  MakeInternals = false
  MapMode = 5
  Placement = pos=(-2e-16,-1.81444,-2e-16) rot=(1,0,0;1.5708rad)
  _ExternalGeoVersion = 1
  sketch-geometry (7):
    g0: LineSegment StartX=-17.1492 StartY=91.9998 StartZ=0 EndX=-33.193 EndY=91.9998 EndZ=0
    g1: LineSegment StartX=-42.62 StartY=93.5589 StartZ=0 EndX=-39.0345 EndY=95.9998 EndZ=0
    g2: LineSegment StartX=-39.0345 StartY=95.9998 StartZ=0 EndX=-17.1492 EndY=95.9998 EndZ=0
    g3: LineSegment StartX=-37.8126 StartY=89.3327 StartZ=0 EndX=-33.193 EndY=91.9998 EndZ=0
    g4: LineSegment StartX=-17.1492 StartY=91.9998 StartZ=0 EndX=-17.1492 EndY=95.9998 EndZ=0
    g5: LineSegment StartX=-42.62 StartY=93.5589 StartZ=0 EndX=-42.62 EndY=91.5589 EndZ=0
    g6: ArcOfCircle CenterX=-39.4391 CenterY=92.1241 CenterZ=0 NormalX=0 NormalY=0 NormalZ=1 AngleXU=0 Radius=3.2307 StartAngle=3.31743 EndAngle=5.23998
  constraints (15):
    c: Horizontal(g0)
    c: Coincident(g1,g2)
    c: Coincident(g3,g0)
    c: Horizontal(g2)
    c: Distance(g2,g0) = 4
    c: Coincident(g2,g-4)
    c: Coincident(g4,g0)
    c: Coincident(g4,g2)
    c: Vertical(g4)
    c: Angle(g3,g0) = 2.61799
    c: Distance(g5) = 2
    c: Vertical(g5)
    c: Coincident(g5,g1)
    c: Coincident(g6,g3)
    c: Coincident(g6,g5)
FEATURE [PartDesign::Pad] Pad016
  BaseFeature = -> Pad015
  Direction = (0,-1,2e-16)
  Length = 10
  Length2 = 10
  Profile = -> Sketch036
  ReferenceAxis = -> Sketch036 [N_Axis]
  Refine = true
  Reversed = true
  SideType = 0
  Suppressed = false
  Type = 0
  Type2 = 0
FEATURE [Sketcher::SketchObject] Sketch037
  ArcFitTolerance = 1e-06
  AttachmentSupport = -> [Pad016]
  ExternalGeometry = -> [Pad016]
  ExternalTypes = [0]
  FullyConstrained = true
  MakeInternals = false
  MapMode = 5
  Placement = pos=(-1.6e-15,-14.6044,-6.3e-15) rot=(1,0,0;1.5708rad)
  _ExternalGeoVersion = 1
  sketch-geometry (9):
    g0: LineSegment StartX=-17.1492 StartY=38.9998 StartZ=0 EndX=-34.1387 EndY=38.9998 EndZ=0
    g1: LineSegment StartX=-34.1387 StartY=38.9998 StartZ=0 EndX=-39.0261 EndY=43.1008 EndZ=0
    g2: LineSegment StartX=-39.0261 StartY=43.1008 StartZ=0 EndX=-38.9632 EndY=43.2479 EndZ=0
    g3: LineSegment StartX=-37.8607 StartY=43.6902 StartZ=0 EndX=-33.6492 EndY=41.8904 EndZ=0
    g4: LineSegment StartX=-33.6492 StartY=41.8904 StartZ=0 EndX=-20.7392 EndY=41.8904 EndZ=0
    g5: LineSegment StartX=-20.7392 StartY=41.8904 StartZ=0 EndX=-17.1492 EndY=44.5827 EndZ=0
    g6: LineSegment StartX=-17.1492 StartY=44.5827 StartZ=0 EndX=-17.1492 EndY=38.9998 EndZ=0
    g7: ArcOfCircle CenterX=-38.1908 CenterY=42.9178 CenterZ=0 NormalX=0 NormalY=0 NormalZ=1 AngleXU=0 Radius=0.84 StartAngle=1.16693 EndAngle=2.73772
    g8: GeomPoint [constr] X=-38.6331 Y=44.0203 Z=0
  constraints (23):
    c: Horizontal(g0)
    c: Coincident(g0,g1)
    c: Coincident(g1,g2)
    c: Coincident(g3,g4)
    c: Parallel(g0,g4)
    c: Coincident(g5,g4)
    c: Coincident(g6,g5)
    c: Coincident(g6,g0)
    c: Perpendicular(g2,g3)
    c: Distance(g2,g8) = 1
    c: PointOnObject(g8,g2)
    c: PointOnObject(g8,g3)
    c: Tangent(g2,g7) = 1.5708
    c: Tangent(g7,g3) = 1.5708
    c: Angle(g4,g3) = 2.73772
    c: Angle(g0,g1) = 2.44346
    c: Distance(g3,g3) = 4.58
    c: Distance(g1,g1) = 6.38
    c: Radius(g7) = 0.84
    c: DistanceX(g5,g5) = 3.59
    c: Coincident(g5,g-3)
    c: Coincident(g0,g-3)
    c: DistanceX(g3,g5) = 16.5
FEATURE [PartDesign::Pad] Pad017
  BaseFeature = -> Pad016
  Direction = (0,-1,2e-16)
  Length = 10
  Length2 = 10
  Profile = -> Sketch037
  ReferenceAxis = -> Sketch037 [N_Axis]
  Refine = true
  Reversed = true
  SideType = 0
  Suppressed = false
  Type = 3
  Type2 = 0
  UpToFace = -> Pad016 [Face129]
FEATURE [Sketcher::SketchObject] Sketch038
  ArcFitTolerance = 1e-06
  AttachmentOffset = pos=(0,0,-13) rot=(0,0,1;0rad)
  ExternalGeometry = -> [Pad016,Pad017]
  ExternalTypes = [0,0]
  FullyConstrained = false
  MakeInternals = false
  MapMode = 5
  Placement = pos=(-1.6e-15,-1.62491,-2e-15) rot=(1,0,0;1.5708rad)
  _ExternalGeoVersion = 1
  sketch-geometry (4):
    g0: LineSegment StartX=-20.7392 StartY=34.1538 StartZ=0 EndX=-81.3647 EndY=34.1538 EndZ=0
    g1: LineSegment StartX=-81.3647 StartY=57.7995 StartZ=0 EndX=-20.7392 EndY=57.7995 EndZ=0
    g2: LineSegment StartX=-81.3647 StartY=57.7995 StartZ=0 EndX=-81.3647 EndY=34.1538 EndZ=0
    g3: LineSegment StartX=-20.7392 StartY=57.7995 StartZ=0 EndX=-20.7392 EndY=34.1538 EndZ=0
  constraints (9):
    c: Horizontal(g0)
    c: Parallel(g0,g1)
    c: Coincident(g2,g1)
    c: Coincident(g2,g0)
    c: Vertical(g2)
    c: Coincident(g3,g1)
    c: Coincident(g3,g0)
    c: Vertical(g3)
    c: PointOnObject(g-4,g3)
FEATURE [PartDesign::Pocket] Pocket017
  BaseFeature = -> Pad017
  Direction = (0,1,2.4e-15)
  Length = 10
  Length2 = 5
  Profile = -> Sketch038
  ReferenceAxis = -> Sketch038 [N_Axis]
  Refine = true
  SideType = 0
  Suppressed = false
  Type = 0
  Type2 = 0
FEATURE [Sketcher::SketchObject] Sketch039
  ArcFitTolerance = 1e-06
  AttachmentOffset = pos=(0,0,-2) rot=(0,0,1;0rad)
  AttachmentSupport = -> [Pocket017]
  ExternalGeometry = -> [Pocket017]
  ExternalTypes = [0,0,0,0]
  FullyConstrained = true
  MakeInternals = false
  MapMode = 5
  Placement = pos=(0,30.4113,4e-16) rot=(0,0.707107,0.707107;3.14159rad)
  _ExternalGeoVersion = 1
  sketch-geometry (4):
    g0: LineSegment StartX=-16.4797 StartY=16.6498 StartZ=0 EndX=31.3391 EndY=28.6498 EndZ=0
    g1: LineSegment StartX=31.3391 StartY=28.6498 StartZ=0 EndX=55.5492 EndY=28.6498 EndZ=0
    g2: LineSegment StartX=55.5492 StartY=28.6498 StartZ=0 EndX=55.5492 EndY=16.6498 EndZ=0
    g3: LineSegment StartX=55.5492 StartY=16.6498 StartZ=0 EndX=-16.4797 EndY=16.6498 EndZ=0
  constraints (11):
    c: Coincident(g0,g1)
    c: Horizontal(g1)
    c: Coincident(g1,g2)
    c: Vertical(g2)
    c: Coincident(g2,g3)
    c: Coincident(g3,g0)
    c: Parallel(g0,g-3)
    c: Distance(g0,g-3) = 2
    c: Distance(g1,g-5) = 2
    c: Distance(g-4,g2) = 1.6
    c: Tangent(g3,g-6)
FEATURE [PartDesign::Pocket] Pocket018
  BaseFeature = -> Pocket017
  Direction = (0,-1,2e-16)
  Length = 54
  Length2 = 5
  Profile = -> Sketch039
  ReferenceAxis = -> Sketch039 [N_Axis]
  Refine = true
  SideType = 0
  Suppressed = false
  Type = 0
  Type2 = 0
FEATURE [PartDesign::Chamfer] Chamfer
  Angle = 45
  Base = -> Pocket018 [Vertex291,Vertex288,Edge431,Edge454,Edge430]
  BaseFeature = -> Pocket018
  ChamferType = 0
  FlipDirection = false
  Refine = true
  Size = 3.5
  Size2 = 1
  SupportTransform = false
  Suppressed = false
  UseAllEdges = false
FEATURE [PartDesign::Chamfer] Chamfer007
  Angle = 45
  Base = -> Chamfer [Edge12,Edge10,Edge91]
  BaseFeature = -> Chamfer
  ChamferType = 0
  FlipDirection = false
  Refine = true
  Size = 3.5
  Size2 = 1
  SupportTransform = false
  Suppressed = false
  UseAllEdges = false
FEATURE [PartDesign::Pocket] Pocket019
  BaseFeature = -> Chamfer007
  Direction = (0,0,1)
  Length = 14
  Length2 = 5
  Profile = -> Sketch030
  ReferenceAxis = -> Sketch030 [N_Axis]
  Refine = true
  SideType = 0
  Suppressed = false
  Type = 0
  Type2 = 0
FEATURE [PartDesign::Pad] Pad018
  BaseFeature = -> Pocket019
  Direction = (0,0,1)
  Length = 4
  Length2 = 10
  Profile = -> Sketch029
  ReferenceAxis = -> Sketch029 [N_Axis]
  Refine = true
  SideType = 0
  Suppressed = false
  Type = 2
  Type2 = 0
FEATURE [Sketcher::SketchObject] Sketch040
  ArcFitTolerance = 1e-06
  ExternalTypes = [0,0,0,0]
  FullyConstrained = false
  MakeInternals = false
  MapMode = 5
  Placement = pos=(-57.1492,3.75e-14,1.895e-13) rot=(0.57735,-0.57735,-0.57735;2.0944rad)
  _ExternalGeoVersion = 1
  sketch-geometry (18):
    g0: LineSegment StartX=-17.0766 StartY=24.5 StartZ=0 EndX=-17.0766 EndY=4.5 EndZ=0
    g1: LineSegment StartX=-17.0766 StartY=4.5 StartZ=0 EndX=10.6234 EndY=4.5 EndZ=0
    g2: LineSegment StartX=10.6234 StartY=4.5 StartZ=0 EndX=10.6234 EndY=24.5 EndZ=0
    g3: LineSegment StartX=10.6234 StartY=24.5 StartZ=0 EndX=-17.0766 EndY=24.5 EndZ=0
    g4: Circle CenterX=-27.1945 CenterY=7.92829 CenterZ=0 NormalX=0 NormalY=0 NormalZ=1 AngleXU=0 Radius=4
    g5: Circle CenterX=20.7413 CenterY=7.92829 CenterZ=0 NormalX=0 NormalY=0 NormalZ=1 AngleXU=0 Radius=4
    g6: LineSegment [constr] StartX=-32.4113 StartY=30.6498 StartZ=0 EndX=-17.0766 EndY=24.5 EndZ=0
    g7: LineSegment [constr] StartX=10.6234 StartY=24.5 StartZ=0 EndX=25.9581 EndY=30.6498 EndZ=0
    g8: LineSegment [constr] StartX=29.5464 StartY=-1.776e-13 StartZ=0 EndX=-35.9996 EndY=-1.918e-13 EndZ=0
    g9: LineSegment [constr] StartX=10.6234 StartY=4.5 StartZ=0 EndX=29.5464 EndY=-1.776e-13 EndZ=0
    g10: LineSegment [constr] StartX=-17.0766 StartY=4.5 StartZ=0 EndX=-35.9996 EndY=-1.918e-13 EndZ=0
    g11: LineSegment [constr] StartX=-17.0766 StartY=4.5 StartZ=0 EndX=-17.0766 EndY=-1.883e-13 EndZ=0
    g12: LineSegment [constr] StartX=10.6234 StartY=4.5 StartZ=0 EndX=20.7413 EndY=7.92829 EndZ=0
    g13: LineSegment [constr] StartX=20.7413 StartY=7.92829 StartZ=0 EndX=29.5464 EndY=-1.776e-13 EndZ=0
    g14: LineSegment [constr] StartX=20.7413 StartY=7.92829 StartZ=0 EndX=10.6234 EndY=24.5 EndZ=0
    g15: LineSegment [constr] StartX=-17.0766 StartY=4.5 StartZ=0 EndX=-27.1945 EndY=7.92829 EndZ=0
    g16: LineSegment [constr] StartX=-27.1945 StartY=7.92829 StartZ=0 EndX=-35.9996 EndY=-1.91e-13 EndZ=0
    g17: LineSegment [constr] StartX=-27.1945 StartY=7.92829 StartZ=0 EndX=-17.0766 EndY=24.5 EndZ=0
  constraints (41):
    c: Coincident(g0,g1)
    c: Coincident(g1,g2)
    c: Coincident(g2,g3)
    c: Coincident(g3,g0)
    c: Vertical(g0)
    c: Vertical(g2)
    c: Horizontal(g1)
    c: Horizontal(g3)
    c: Diameter(g4) = 8
    c: Diameter(g5) = 8
    c: DistanceY(g0,g0) = 20
    c: DistanceX(g3,g3) = 27.7
    c: Coincident(g6,g-3)
    c: Coincident(g6,g0)
    c: Coincident(g7,g2)
    c: Coincident(g7,g-3)
    c: Equal(g6,g7)
    c: Coincident(g8,g-5)
    c: Coincident(g8,g-4)
    c: Coincident(g9,g1)
    c: Coincident(g9,g8)
    c: Coincident(g10,g0)
    c: Coincident(g10,g8)
    c: Coincident(g11,g0)
    c: PointOnObject(g11,g8)
    c: Vertical(g11)
    c: DistanceY(g11,g11) = 4.5
    c: Coincident(g12,g1)
    c: Coincident(g12,g5)
    c: Coincident(g13,g5)
    c: Coincident(g13,g8)
    c: Coincident(g14,g5)
    c: Coincident(g14,g2)
    c: Coincident(g15,g0)
    c: Coincident(g15,g4)
    c: Coincident(g16,g4)
    c: Coincident(g16,g8)
    c: Coincident(g17,g4)
    c: Coincident(g17,g0)
    c: Equal(g12,g15)
    c: Equal(g16,g13)
FEATURE [PartDesign::Body] Body001  label="Body"
  AllowCompound = false
  Group = -> [Binder001,Sketch010,Pad003,Sketch011,Pad004,Sketch013,Pocket008,Sketch014,Pocket009,Chamfer004,Sketch015,Pad005,Sketch025,Pocket013,LinearPattern,Hole,Sketch027,Pocket014,Pad013,Pocket016,Sketch028,Sketch031,Sketch032,Sketch034,Pad014,Sketch035,Pad015,Sketch036,Pad016,Sketch037,Pad017,Sketch038,Pocket017,Sketch039,Pocket018,Chamfer,Chamfer007,Sketch030,Sketch029,Pocket019,Pad018,Sketch040,+15 more]
  Origin = -> Origin
  Tip = -> Chamfer010
COMPONENT P3 — recipe-attached ("logo-outline", modeled in this document).
Construction recipe (the document's own serialized feature program — sketch geometry with constraints, then the solid features built on it; lengths are millimeters unless a unit is written):

FEATURE [Sketcher::SketchObject] Sketch021
  ArcFitTolerance = 1e-06
  AttachmentOffset = pos=(-27,-21,40.75) rot=(0,1,0;0rad)
  AttachmentSupport = -> [XZ_Plane]
  ExternalTypes = [0]
  FullyConstrained = false
  MakeInternals = false
  MapMode = 5
  Placement = pos=(-27,-40.75,-21) rot=(1,0,0;1.5708rad)
  _ExternalGeoVersion = 0
  sketch-geometry (10):
    g0: LineSegment StartX=16.4753 StartY=20.5288 StartZ=0 EndX=25.4753 EndY=20.5288 EndZ=0
    g1: LineSegment StartX=28.4753 StartY=23.5288 StartZ=0 EndX=28.4753 EndY=32.5288 EndZ=0
    g2: LineSegment StartX=25.4753 StartY=35.5288 StartZ=0 EndX=16.4753 EndY=35.5288 EndZ=0
    g3: LineSegment StartX=13.4753 StartY=32.5288 StartZ=0 EndX=13.4753 EndY=23.5288 EndZ=0
    g4: ArcOfCircle CenterX=16.4753 CenterY=23.5288 CenterZ=0 NormalX=0 NormalY=0 NormalZ=1 AngleXU=0 Radius=3 StartAngle=3.14159 EndAngle=4.71239
    g5: ArcOfCircle CenterX=25.4753 CenterY=23.5288 CenterZ=0 NormalX=0 NormalY=0 NormalZ=1 AngleXU=0 Radius=3 StartAngle=4.71239 EndAngle=6.28319
    g6: ArcOfCircle CenterX=25.4753 CenterY=32.5288 CenterZ=0 NormalX=0 NormalY=0 NormalZ=1 AngleXU=0 Radius=3 StartAngle=0 EndAngle=1.5708
    g7: ArcOfCircle CenterX=16.4753 CenterY=32.5288 CenterZ=0 NormalX=0 NormalY=0 NormalZ=1 AngleXU=0 Radius=3 StartAngle=1.5708 EndAngle=3.14159
    g8: GeomPoint [constr] X=13.4753 Y=20.5288 Z=0
    g9: GeomPoint [constr] X=28.4753 Y=35.5288 Z=0
  constraints (22):
    c: Tangent(g0,g4) = -1.5708
    c: Tangent(g0,g5) = -1.5708
    c: Tangent(g1,g5) = -1.5708
    c: Tangent(g1,g6) = -1.5708
    c: Tangent(g2,g6) = -1.5708
    c: Tangent(g2,g7) = -1.5708
    c: Tangent(g3,g7) = -1.5708
    c: Tangent(g3,g4) = -1.5708
    c: Horizontal(g0)
    c: Horizontal(g2)
    c: Vertical(g1)
    c: Vertical(g3)
    c: Equal(g4,g5)
    c: Equal(g5,g6)
    c: Equal(g6,g7)
    c: PointOnObject(g8,g0)
    c: PointOnObject(g8,g3)
    c: PointOnObject(g9,g1)
    c: PointOnObject(g9,g2)
    c: Distance(g1,g3) = 15
    c: Distance(g0,g2) = 15
    c: Radius(g5) = 3
FEATURE [PartDesign::Pad] Pad008
  Direction = (0,-1,2e-16)
  Length = 1
  Length2 = 10
  Placement = pos=(0,0,0) rot=(1,0,0;1.5708rad)
  Profile = -> Sketch021
  ReferenceAxis = -> Sketch021 [N_Axis]
  Refine = true
  Reversed = true
  SideType = 0
  Suppressed = false
  Type = 0
  Type2 = 0
FEATURE [PartDesign::Body] Body002  label="logo-outline"
  AllowCompound = false
  Group = -> [Sketch021,Pad008]
  Origin = -> Origin062
  Tip = -> Pad008
COMPONENT P4 — recipe-attached ("logo-controller", modeled in this document).
Construction recipe (the document's own serialized feature program — sketch geometry with constraints, then the solid features built on it; lengths are millimeters unless a unit is written):

FEATURE [PartDesign::SubShapeBinder] Binder002
  BindCopyOnChange = 0
  BindMode = 0
  ClaimChildren = false
  Context = -> Body003 [Binder002.]
  Fuse = false
  MakeFace = true
  OffsetFill = false
  OffsetIntersection = false
  OffsetJoinType = 0
  OffsetOpenResult = false
  PartialLoad = false
  Refine = true
  Relative = true
  Support = -> [Body002,Sketch022]
  _Version = 2
FEATURE [Sketcher::SketchObject] Sketch022
  ArcFitTolerance = 1e-06
  AttachmentOffset = pos=(-8.4,-58.5,40.75) rot=(0,0,-1;1.5708rad)
  AttachmentSupport = -> [XZ_Plane063]
  ExternalTypes = [0]
  FullyConstrained = false
  MakeInternals = false
  MapMode = 5
  Placement = pos=(-8.4,-40.75,-58.5) rot=(0.57735,0.57735,-0.57735;2.0944rad)
  _ExternalGeoVersion = 0
  sketch-geometry (18):
    g0: BSplineCurve PolesCount=2 KnotsCount=2 Degree=1 IsPeriodic=0
    g1: BSplineCurve PolesCount=4 KnotsCount=2 Degree=3 IsPeriodic=0
    g2: BSplineCurve PolesCount=4 KnotsCount=2 Degree=3 IsPeriodic=0
    g3: BSplineCurve PolesCount=4 KnotsCount=2 Degree=3 IsPeriodic=0
    g4: BSplineCurve PolesCount=4 KnotsCount=2 Degree=3 IsPeriodic=0
    g5: BSplineCurve PolesCount=4 KnotsCount=2 Degree=3 IsPeriodic=0
    g6: BSplineCurve PolesCount=4 KnotsCount=2 Degree=3 IsPeriodic=0
    g7: BSplineCurve PolesCount=2 KnotsCount=2 Degree=1 IsPeriodic=0
    g8: BSplineCurve PolesCount=2 KnotsCount=2 Degree=1 IsPeriodic=0
    g9: BSplineCurve PolesCount=2 KnotsCount=2 Degree=1 IsPeriodic=0
    g10: BSplineCurve PolesCount=4 KnotsCount=2 Degree=3 IsPeriodic=0
    g11: BSplineCurve PolesCount=4 KnotsCount=2 Degree=3 IsPeriodic=0
    g12: BSplineCurve PolesCount=4 KnotsCount=2 Degree=3 IsPeriodic=0
    g13: BSplineCurve PolesCount=4 KnotsCount=2 Degree=3 IsPeriodic=0
    g14: BSplineCurve PolesCount=2 KnotsCount=2 Degree=1 IsPeriodic=0
    g15: BSplineCurve PolesCount=4 KnotsCount=2 Degree=3 IsPeriodic=0
    g16: BSplineCurve PolesCount=2 KnotsCount=2 Degree=1 IsPeriodic=0
    g17: BSplineCurve PolesCount=2 KnotsCount=2 Degree=1 IsPeriodic=0
  constraints (18):
    c: Coincident(g0,g1)
    c: Coincident(g1,g2)
    c: Coincident(g2,g3)
    c: Coincident(g3,g4)
    c: Coincident(g4,g5)
    c: Coincident(g5,g6)
    c: Coincident(g6,g7)
    c: Coincident(g7,g8)
    c: Coincident(g8,g9)
    c: Coincident(g9,g10)
    c: Coincident(g10,g11)
    c: Coincident(g11,g12)
    c: Coincident(g12,g13)
    c: Coincident(g13,g14)
    c: Coincident(g14,g15)
    c: Coincident(g15,g16)
    c: Coincident(g16,g17)
    c: Coincident(g17,g0)
FEATURE [PartDesign::Pad] Pad009
  Direction = (0,-1,2e-16)
  Length = 1
  Length2 = 10
  Placement = pos=(0,0,0) rot=(1,0,0;1.5708rad)
  Profile = -> Sketch022
  ReferenceAxis = -> Sketch022 [N_Axis]
  Refine = true
  Reversed = true
  SideType = 0
  Suppressed = false
  Type = 0
  Type2 = 0
FEATURE [PartDesign::Body] Body003  label="logo-controller"
  AllowCompound = false
  Group = -> [Binder002,Sketch022,Pad009]
  Origin = -> Origin063
  Tip = -> Pad009
COMPONENT P5 — recipe-attached ("logo-led", modeled in this document).
Construction recipe (the document's own serialized feature program — sketch geometry with constraints, then the solid features built on it; lengths are millimeters unless a unit is written):

FEATURE [PartDesign::SubShapeBinder] Binder003
  BindCopyOnChange = 0
  BindMode = 0
  ClaimChildren = false
  Context = -> Body004 [Binder003.]
  Fuse = false
  MakeFace = true
  OffsetFill = false
  OffsetIntersection = false
  OffsetJoinType = 0
  OffsetOpenResult = false
  PartialLoad = false
  Refine = true
  Relative = true
  Support = -> [Body003,Body002]
  _Version = 2
FEATURE [Sketcher::SketchObject] Sketch023
  ArcFitTolerance = 1e-06
  AttachmentOffset = pos=(-5,0.5,40.75) rot=(0,0,1;0rad)
  AttachmentSupport = -> [XZ_Plane064]
  ExternalGeometry = -> [Binder003]
  ExternalTypes = [0]
  FullyConstrained = false
  MakeInternals = false
  MapMode = 5
  Placement = pos=(-5,-40.75,0.5) rot=(1,0,0;1.5708rad)
  _ExternalGeoVersion = 0
  sketch-geometry (4):
    g0: LineSegment StartX=1.04202 StartY=6.13059 StartZ=0 EndX=1.04202 EndY=2.24552 EndZ=0
    g1: ArcOfCircle CenterX=-0.971817 CenterY=2.24552 CenterZ=0 NormalX=0 NormalY=0 NormalZ=1 AngleXU=0 Radius=2.01384 StartAngle=3.14159 EndAngle=6.28319
    g2: LineSegment StartX=-2.98566 StartY=2.24552 StartZ=0 EndX=-2.98566 EndY=6.13059 EndZ=0
    g3: LineSegment StartX=-2.98566 StartY=6.13059 StartZ=0 EndX=1.04202 EndY=6.13059 EndZ=0
  constraints (7):
    c: Vertical(g0)
    c: Tangent(g0,g1) = 1.5708
    c: Tangent(g1,g2) = 1.5708
    c: Horizontal(g1,g0)
    c: Coincident(g3,g2)
    c: Coincident(g3,g0)
    c: Horizontal(g3)
FEATURE [PartDesign::Pad] Pad010
  Direction = (0,-1,2e-16)
  Length = 1
  Length2 = 10
  Placement = pos=(0,0,0) rot=(1,0,0;1.5708rad)
  Profile = -> Sketch023
  ReferenceAxis = -> Sketch023 [N_Axis]
  Refine = true
  Reversed = true
  SideType = 0
  Suppressed = false
  Type = 0
  Type2 = 0
FEATURE [PartDesign::Body] Body004  label="logo-led"
  AllowCompound = false
  Group = -> [Binder003,Sketch023,Pad010]
  Origin = -> Origin064
  Tip = -> Pad010
COMPONENT P6 — recipe-attached ("logo-led-outline", modeled in this document).
Construction recipe (the document's own serialized feature program — sketch geometry with constraints, then the solid features built on it; lengths are millimeters unless a unit is written):

FEATURE [PartDesign::SubShapeBinder] Binder004
  BindCopyOnChange = 0
  BindMode = 0
  ClaimChildren = false
  Context = -> Body005 [Binder004.]
  Fuse = false
  MakeFace = true
  OffsetFill = false
  OffsetIntersection = false
  OffsetJoinType = 0
  OffsetOpenResult = false
  PartialLoad = false
  Refine = true
  Relative = true
  Support = -> [Body004]
  _Version = 2
FEATURE [Sketcher::SketchObject] Sketch026
  ArcFitTolerance = 1e-06
  AttachmentOffset = pos=(-5,0.5,40.75) rot=(0,0,1;0rad)
  AttachmentSupport = -> [XZ_Plane065]
  ExternalGeometry = -> [Binder004]
  ExternalTypes = [0]
  FullyConstrained = false
  MakeInternals = false
  MapMode = 5
  Placement = pos=(-5,-40.75,0.5) rot=(1,0,0;1.5708rad)
  _ExternalGeoVersion = 0
  sketch-geometry (4):
    g0: LineSegment StartX=1.34829 StartY=2.22498 StartZ=0 EndX=1.34829 EndY=6.38734 EndZ=0
    g1: LineSegment StartX=1.34829 StartY=6.38734 StartZ=0 EndX=-3.31566 EndY=6.38734 EndZ=0
    g2: LineSegment StartX=-3.31566 StartY=6.38734 StartZ=0 EndX=-3.31566 EndY=2.22498 EndZ=0
    g3: ArcOfCircle CenterX=-0.983687 CenterY=2.22498 CenterZ=0 NormalX=0 NormalY=0 NormalZ=1 AngleXU=0 Radius=2.33197 StartAngle=3.14159 EndAngle=6.28318
  constraints (4):
    c: Coincident(g0,g1)
    c: Coincident(g1,g2)
    c: Tangent(g2,g3) = -1.5708
    c: Coincident(g3,g0)
FEATURE [PartDesign::Pad] Pad011
  Direction = (0,-1,2e-16)
  Length = 1
  Length2 = 10
  Placement = pos=(0,0,0) rot=(1,0,0;1.5708rad)
  Profile = -> Sketch026
  ReferenceAxis = -> Sketch026 [N_Axis]
  Refine = true
  Reversed = true
  SideType = 0
  Suppressed = false
  Type = 0
  Type2 = 0
FEATURE [PartDesign::Body] Body005  label="logo-led-outline"
  AllowCompound = false
  Group = -> [Binder004,Sketch026,Pad011]
  Origin = -> Origin065
  Tip = -> Pad011
COMPONENT P7 — recipe-attached ("logo-controller-button", modeled in this document).
Construction recipe (the document's own serialized feature program — sketch geometry with constraints, then the solid features built on it; lengths are millimeters unless a unit is written):

FEATURE [Sketcher::SketchObject] Sketch043
  ArcFitTolerance = 1e-06
  AttachmentOffset = pos=(-10,0,40.75) rot=(0,0,1;0rad)
  AttachmentSupport = -> [Origin101]
  ExternalTypes = [0]
  FullyConstrained = false
  MakeInternals = false
  MapMode = 5
  Placement = pos=(-10,-40.75,9e-15) rot=(1,0,0;1.5708rad)
  _ExternalGeoVersion = 1
  sketch-geometry (1):
    g0: Circle CenterX=1.43804 CenterY=10.3162 CenterZ=0 NormalX=0 NormalY=0 NormalZ=1 AngleXU=0 Radius=0.735815
FEATURE [PartDesign::Pad] Pad020
  Direction = (0,-1,2e-16)
  Length = 1
  Length2 = 10
  Profile = -> Sketch043
  ReferenceAxis = -> Sketch043 [N_Axis]
  Refine = true
  Reversed = true
  SideType = 0
  Suppressed = false
  Type = 0
  Type2 = 0
FEATURE [PartDesign::Body] Body006  label="logo-controller-button"
  AllowCompound = false
  Group = -> [Sketch043,Pad020]
  Origin = -> Origin101
  Tip = -> Pad020
COMPONENT P8 — recipe-attached ("logo-controller-d-pad", modeled in this document).
Construction recipe (the document's own serialized feature program — sketch geometry with constraints, then the solid features built on it; lengths are millimeters unless a unit is written):

FEATURE [Sketcher::SketchObject] Sketch044
  ArcFitTolerance = 1e-06
  AttachmentOffset = pos=(0,0,40.75) rot=(0,0,1;0rad)
  AttachmentSupport = -> [Origin103]
  ExternalTypes = [0]
  FullyConstrained = false
  MakeInternals = false
  MapMode = 5
  Placement = pos=(0,-40.75,9e-15) rot=(1,0,0;1.5708rad)
  _ExternalGeoVersion = 1
  sketch-geometry (15):
    g0: LineSegment StartX=-3.01409 StartY=9.17394 StartZ=0 EndX=-3.01409 EndY=9.92394 EndZ=0
    g1: LineSegment StartX=-3.01409 StartY=11.1739 StartZ=0 EndX=-3.51409 EndY=11.1739 EndZ=0
    g2: LineSegment StartX=-3.51409 StartY=11.1739 StartZ=0 EndX=-3.51409 EndY=10.4239 EndZ=0
    g3: LineSegment StartX=-3.51409 StartY=9.17394 StartZ=0 EndX=-3.01409 EndY=9.17394 EndZ=0
    g4: LineSegment StartX=-2.26409 StartY=9.92394 StartZ=0 EndX=-2.26409 EndY=10.4239 EndZ=0
    g5: LineSegment StartX=-2.26409 StartY=10.4239 StartZ=0 EndX=-3.01409 EndY=10.4239 EndZ=0
    g6: LineSegment StartX=-4.26409 StartY=10.4239 StartZ=0 EndX=-4.26409 EndY=9.92394 EndZ=0
    g7: LineSegment StartX=-4.26409 StartY=9.92394 StartZ=0 EndX=-3.51409 EndY=9.92394 EndZ=0
    g8: LineSegment [constr] StartX=-3.01409 StartY=9.17394 StartZ=0 EndX=-2.26409 EndY=9.92394 EndZ=0
    g9: LineSegment [constr] StartX=-4.26409 StartY=10.4239 StartZ=0 EndX=-3.51409 EndY=11.1739 EndZ=0
    g10: LineSegment [constr] StartX=-3.01409 StartY=11.1739 StartZ=0 EndX=-2.26409 EndY=10.4239 EndZ=0
    g11: LineSegment StartX=-3.01409 StartY=9.92394 StartZ=0 EndX=-2.26409 EndY=9.92394 EndZ=0
    g12: LineSegment StartX=-3.01409 StartY=10.4239 StartZ=0 EndX=-3.01409 EndY=11.1739 EndZ=0
    g13: LineSegment StartX=-3.51409 StartY=10.4239 StartZ=0 EndX=-4.26409 EndY=10.4239 EndZ=0
    g14: LineSegment StartX=-3.51409 StartY=9.92394 StartZ=0 EndX=-3.51409 EndY=9.17394 EndZ=0
  constraints (40):
    c: Coincident(g12,g1)
    c: Coincident(g1,g2)
    c: Coincident(g14,g3)
    c: Coincident(g3,g0)
    c: Horizontal(g1)
    c: Horizontal(g3)
    c: Distance(g0,g14) = 0.5
    c: Distance(g1,g3) = 2
    c: Coincident(g4,g5)
    c: Coincident(g13,g6)
    c: Coincident(g6,g7)
    c: Coincident(g11,g4)
    c: Vertical(g4)
    c: Vertical(g6)
    c: Distance(g4,g6) = 2
    c: Distance(g5,g11) = 0.5
    c: Coincident(g8,g0)
    c: Coincident(g8,g4)
    c: Coincident(g9,g13)
    c: Coincident(g9,g1)
    c: Coincident(g10,g12)
    c: Coincident(g10,g4)
    c: Equal(g8,g10)
    c: Equal(g8,g9)
    c: Horizontal(g7)
    c: Horizontal(g11)
    c: Vertical(g0)
    c: Vertical(g12)
    c: Coincident(g11,g0)
    c: Horizontal(g5)
    c: Horizontal(g13)
    c: Coincident(g12,g5)
    c: Vertical(g2)
    c: Vertical(g14)
    c: Coincident(g7,g14)
    c: Coincident(g13,g2)
    c: Vertical(g0,g5)
    c: Vertical(g7,g2)
    c: Horizontal(g7,g0)
    c: Horizontal(g2,g5)
FEATURE [PartDesign::Pad] Pad021
  Direction = (0,-1,2e-16)
  Length = 1
  Length2 = 10
  Profile = -> Sketch044
  ReferenceAxis = -> Sketch044 [N_Axis]
  Refine = true
  Reversed = true
  SideType = 0
  Suppressed = false
  Type = 0
  Type2 = 0
FEATURE [PartDesign::Body] Body007  label="logo-controller-d-pad"
  AllowCompound = false
  Group = -> [Sketch044,Pad021]
  Origin = -> Origin103
  Tip = -> Pad021
PROVENANCE & LICENSES
A FreeCAD (.FCStd) document from a public repository crawl; recipes are the document's own serialized feature recipes (and, for linked parts, companion documents' recipes).
License: mit.
